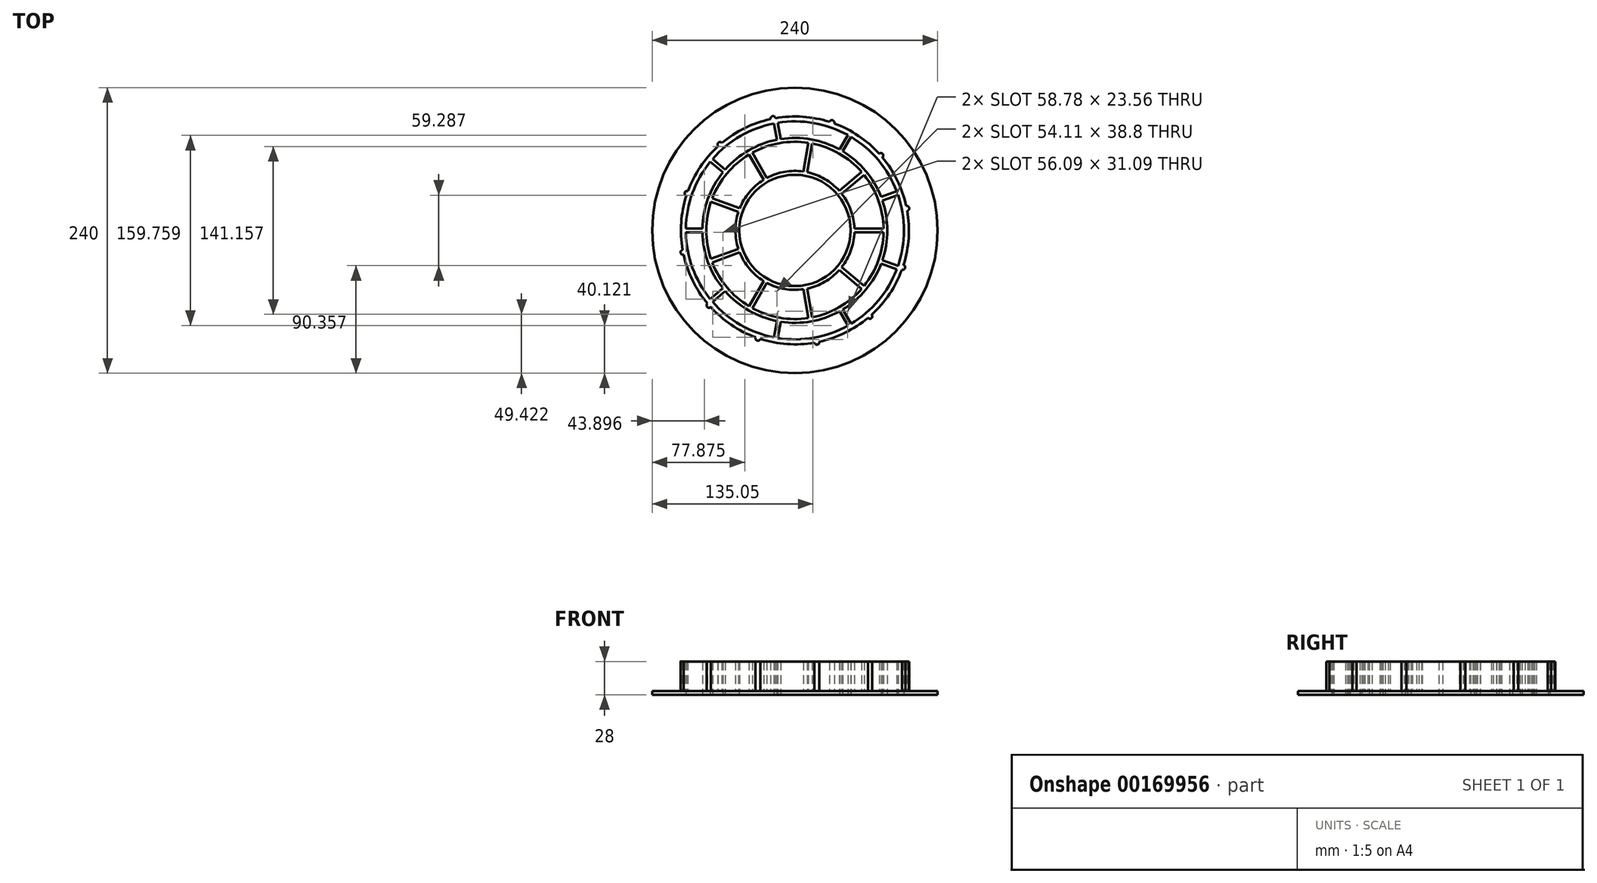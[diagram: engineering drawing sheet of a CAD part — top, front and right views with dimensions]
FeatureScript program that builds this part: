
annotation { "Feature Type Name" : "Feature", "Feature Type Description" : "" }
export const myFeature = defineFeature(function(context is Context, id is Id, definition is map)
    precondition{}
    {
        {
            var Q0;
            Q0=qCreatedBy(makeId("Top.planeOp"),FACE);
            var sketch = newSketch(context, id + "F0", { "sketchPlane" : qUnion([Q0])});
            skCircle(sketch, "E0", {"center": v(0, 0) * mm, "radius": 46.79 * mm});
            skCircle(sketch, "E1.0", {"center": v(0, 0) * mm, "radius": 49.98 * mm});
            skCircle(sketch, "E2", {"center": v(0, 0) * mm, "radius": 74.53 * mm});
            skCircle(sketch, "E3.0", {"center": v(0, 0) * mm, "radius": 77.73 * mm});
            skCircle(sketch, "E4", {"center": v(0, 0) * mm, "radius": 91.66 * mm});
            skCircle(sketch, "E5.0", {"center": v(0, 0) * mm, "radius": 95.78 * mm});
            skCircle(sketch, "E6", {"center": v(0, 0) * mm, "radius": 120 * mm});
            skLineSegment(sketch, "E7", {"start": v(46.79, 0) * mm, "end": v(77.72, 0) * mm, "construction": true});
            skLineSegment(sketch, "E8.0", {"start": v(46.79, -1.6) * mm, "end": v(77.99, -1.6) * mm});
            skLineSegment(sketch, "E9.0", {"start": v(46.79, 1.6) * mm, "end": v(77.99, 1.6) * mm});
            skLineSegment(sketch, "E10.1.0", {"start": v(34.81, 31.3) * mm, "end": v(58.71, 51.35) * mm});
            skLineSegment(sketch, "E10.1.1", {"start": v(35.84, 30.07) * mm, "end": v(59.54, 49.96) * mm, "construction": true});
            skLineSegment(sketch, "E10.1.2", {"start": v(36.87, 28.85) * mm, "end": v(60.77, 48.9) * mm});
            skLineSegment(sketch, "E10.2.0", {"start": v(6.55, 46.35) * mm, "end": v(11.97, 77.08) * mm});
            skLineSegment(sketch, "E10.2.1", {"start": v(8.12, 46.07) * mm, "end": v(13.5, 76.54) * mm, "construction": true});
            skLineSegment(sketch, "E10.2.2", {"start": v(9.7, 45.8) * mm, "end": v(15.12, 76.52) * mm});
            skLineSegment(sketch, "E10.3.0", {"start": v(-24.78, 39.72) * mm, "end": v(-40.38, 66.74) * mm});
            skLineSegment(sketch, "E10.3.1", {"start": v(-23.4, 40.52) * mm, "end": v(-38.86, 67.31) * mm, "construction": true});
            skLineSegment(sketch, "E10.3.2", {"start": v(-22, 41.32) * mm, "end": v(-37.6, 68.34) * mm});
            skLineSegment(sketch, "E10.4.0", {"start": v(-44.51, 14.5) * mm, "end": v(-73.83, 25.17) * mm});
            skLineSegment(sketch, "E10.4.1", {"start": v(-43.96, 16) * mm, "end": v(-73.04, 26.58) * mm, "construction": true});
            skLineSegment(sketch, "E10.4.2", {"start": v(-43.42, 17.5) * mm, "end": v(-72.74, 28.18) * mm});
            skLineSegment(sketch, "E10.5.0", {"start": v(-43.42, -17.5) * mm, "end": v(-72.74, -28.18) * mm});
            skLineSegment(sketch, "E10.5.1", {"start": v(-43.96, -16) * mm, "end": v(-73.04, -26.58) * mm, "construction": true});
            skLineSegment(sketch, "E10.5.2", {"start": v(-44.51, -14.5) * mm, "end": v(-73.83, -25.17) * mm});
            skLineSegment(sketch, "E10.6.0", {"start": v(-22, -41.32) * mm, "end": v(-37.6, -68.34) * mm});
            skLineSegment(sketch, "E10.6.1", {"start": v(-23.4, -40.52) * mm, "end": v(-38.86, -67.31) * mm, "construction": true});
            skLineSegment(sketch, "E10.6.2", {"start": v(-24.78, -39.72) * mm, "end": v(-40.38, -66.74) * mm});
            skLineSegment(sketch, "E10.7.0", {"start": v(9.7, -45.8) * mm, "end": v(15.12, -76.52) * mm});
            skLineSegment(sketch, "E10.7.1", {"start": v(8.12, -46.07) * mm, "end": v(13.5, -76.54) * mm, "construction": true});
            skLineSegment(sketch, "E10.7.2", {"start": v(6.55, -46.35) * mm, "end": v(11.97, -77.08) * mm});
            skLineSegment(sketch, "E10.8.0", {"start": v(36.87, -28.85) * mm, "end": v(60.77, -48.9) * mm});
            skLineSegment(sketch, "E10.8.1", {"start": v(35.84, -30.07) * mm, "end": v(59.54, -49.96) * mm, "construction": true});
            skLineSegment(sketch, "E10.8.2", {"start": v(34.81, -31.3) * mm, "end": v(58.71, -51.35) * mm});
            skPoint(sketch, "E11.center", {"position": v(-0.02, 0.04) * mm});
            skLineSegment(sketch, "E12", {"start": v(57.09, 47.9) * mm, "end": v(73.38, 61.57) * mm, "construction": true});
            skLineSegment(sketch, "E13.0", {"start": v(58.22, 46.76) * mm, "end": v(74.6, 60.51) * mm});
            skLineSegment(sketch, "E14.0", {"start": v(56.16, 49.21) * mm, "end": v(72.55, 62.96) * mm});
            skLineSegment(sketch, "E15.1.0", {"start": v(35.94, 65.45) * mm, "end": v(46.64, 83.98) * mm});
            skLineSegment(sketch, "E15.1.1", {"start": v(38.71, 63.85) * mm, "end": v(49.4, 82.38) * mm});
            skLineSegment(sketch, "E15.2.0", {"start": v(11.39, 73.8) * mm, "end": v(15.1, 94.86) * mm});
            skLineSegment(sketch, "E15.2.1", {"start": v(14.54, 73.24) * mm, "end": v(18.25, 94.3) * mm});
            skLineSegment(sketch, "E15.3.0", {"start": v(-14.54, 73.24) * mm, "end": v(-18.25, 94.3) * mm});
            skLineSegment(sketch, "E15.3.1", {"start": v(-11.39, 73.8) * mm, "end": v(-15.1, 94.86) * mm});
            skLineSegment(sketch, "E15.4.0", {"start": v(-38.71, 63.85) * mm, "end": v(-49.4, 82.38) * mm});
            skLineSegment(sketch, "E15.4.1", {"start": v(-35.94, 65.45) * mm, "end": v(-46.64, 83.98) * mm});
            skLineSegment(sketch, "E15.5.0", {"start": v(-58.22, 46.76) * mm, "end": v(-74.6, 60.51) * mm});
            skLineSegment(sketch, "E15.5.1", {"start": v(-56.16, 49.21) * mm, "end": v(-72.55, 62.96) * mm});
            skLineSegment(sketch, "E15.6.0", {"start": v(-70.7, 24.03) * mm, "end": v(-90.8, 31.35) * mm});
            skLineSegment(sketch, "E15.6.1", {"start": v(-69.6, 27.04) * mm, "end": v(-89.7, 34.35) * mm});
            skLineSegment(sketch, "E15.7.0", {"start": v(-74.66, -1.6) * mm, "end": v(-96.05, -1.6) * mm});
            skLineSegment(sketch, "E15.7.1", {"start": v(-74.66, 1.6) * mm, "end": v(-96.05, 1.6) * mm});
            skLineSegment(sketch, "E15.8.0", {"start": v(-69.6, -27.04) * mm, "end": v(-89.7, -34.35) * mm});
            skLineSegment(sketch, "E15.8.1", {"start": v(-70.7, -24.03) * mm, "end": v(-90.8, -31.35) * mm});
            skLineSegment(sketch, "E15.9.0", {"start": v(-56.16, -49.21) * mm, "end": v(-72.55, -62.96) * mm});
            skLineSegment(sketch, "E15.9.1", {"start": v(-58.22, -46.76) * mm, "end": v(-74.6, -60.51) * mm});
            skLineSegment(sketch, "E15.10.0", {"start": v(-35.94, -65.45) * mm, "end": v(-46.64, -83.98) * mm});
            skLineSegment(sketch, "E15.10.1", {"start": v(-38.71, -63.85) * mm, "end": v(-49.4, -82.38) * mm});
            skLineSegment(sketch, "E15.11.0", {"start": v(-11.39, -73.8) * mm, "end": v(-15.1, -94.86) * mm});
            skLineSegment(sketch, "E15.11.1", {"start": v(-14.54, -73.24) * mm, "end": v(-18.25, -94.3) * mm});
            skLineSegment(sketch, "E15.12.0", {"start": v(14.54, -73.24) * mm, "end": v(18.25, -94.3) * mm});
            skLineSegment(sketch, "E15.12.1", {"start": v(11.39, -73.8) * mm, "end": v(15.1, -94.86) * mm});
            skLineSegment(sketch, "E15.13.0", {"start": v(38.71, -63.85) * mm, "end": v(49.4, -82.38) * mm});
            skLineSegment(sketch, "E15.13.1", {"start": v(35.94, -65.45) * mm, "end": v(46.64, -83.98) * mm});
            skLineSegment(sketch, "E15.14.0", {"start": v(58.22, -46.76) * mm, "end": v(74.6, -60.51) * mm});
            skLineSegment(sketch, "E15.14.1", {"start": v(56.16, -49.21) * mm, "end": v(72.55, -62.96) * mm});
            skLineSegment(sketch, "E15.15.0", {"start": v(70.7, -24.03) * mm, "end": v(90.8, -31.35) * mm});
            skLineSegment(sketch, "E15.15.1", {"start": v(69.6, -27.04) * mm, "end": v(89.7, -34.35) * mm});
            skLineSegment(sketch, "E15.16.0", {"start": v(74.66, 1.6) * mm, "end": v(96.05, 1.6) * mm});
            skLineSegment(sketch, "E15.16.1", {"start": v(74.66, -1.6) * mm, "end": v(96.05, -1.6) * mm});
            skLineSegment(sketch, "E15.17.0", {"start": v(69.6, 27.04) * mm, "end": v(89.7, 34.35) * mm});
            skLineSegment(sketch, "E15.17.1", {"start": v(70.7, 24.03) * mm, "end": v(90.8, 31.35) * mm});
            skCircle(sketch, "E16", {"center": v(94, 18.42) * mm, "radius": 2.1 * mm});
            skCircle(sketch, "E17.1.0", {"center": v(72.2, 62.95) * mm, "radius": 2.1 * mm});
            skCircle(sketch, "E17.2.0", {"center": v(31.04, 90.61) * mm, "radius": 2.1 * mm});
            skCircle(sketch, "E17.3.0", {"center": v(-18.42, 94) * mm, "radius": 2.1 * mm});
            skCircle(sketch, "E17.4.0", {"center": v(-62.95, 72.2) * mm, "radius": 2.1 * mm});
            skCircle(sketch, "E17.5.0", {"center": v(-90.61, 31.04) * mm, "radius": 2.1 * mm});
            skCircle(sketch, "E17.6.0", {"center": v(-94, -18.42) * mm, "radius": 2.1 * mm});
            skCircle(sketch, "E17.7.0", {"center": v(-72.2, -62.95) * mm, "radius": 2.1 * mm});
            skCircle(sketch, "E17.8.0", {"center": v(-31.04, -90.61) * mm, "radius": 2.1 * mm});
            skCircle(sketch, "E17.9.0", {"center": v(18.42, -94) * mm, "radius": 2.1 * mm});
            skCircle(sketch, "E17.10.0", {"center": v(62.95, -72.2) * mm, "radius": 2.1 * mm});
            skCircle(sketch, "E17.11.0", {"center": v(90.61, -31.04) * mm, "radius": 2.1 * mm});
            skSolve(sketch);
        }
        {
            var Q0;
            {var subQ0=sQuery(id+"F0.wireOp",EDGE,"E8.0");var subQ1=sQuery(id+"F0.wireOp",EDGE,"E2");var subQ2=makeQuery(id+"F0.imprint","INTERSECT",VERTEX,{"derivedFrom":[subQ1,subQ0]});Q0=makeQuery(id+"F0.imprint","IMPRINT",FACE,{"disambiguationData":[TD([[makeQuery(id+"F0.imprint","IMPRINT",EDGE,{"disambiguationData":[TD([[subQ2,1.0]])],"derivedFrom":subQ1}),-1.0]])]});}
            var Q1;
            Q1=makeQuery(id+"F0.imprint","IMPRINT",FACE,{"disambiguationData":[TD([[makeQuery(id+"F0.imprint","IMPRINT",EDGE,{"derivedFrom":sQuery(id+"F0.wireOp",EDGE,"E4")}),-1.0]])]});
            var Q2;
            {var subQ0=sQuery(id+"F0.wireOp",EDGE,"E8.0");var subQ1=sQuery(id+"F0.wireOp",EDGE,"E2");var subQ2=makeQuery(id+"F0.imprint","INTERSECT",VERTEX,{"derivedFrom":[subQ1,subQ0]});Q2=makeQuery(id+"F0.imprint","IMPRINT",FACE,{"disambiguationData":[TD([[makeQuery(id+"F0.imprint","IMPRINT",EDGE,{"disambiguationData":[TD([[subQ2,-1.0]])],"derivedFrom":subQ1}),-1.0]])]});}
            var Q3;
            {var subQ0=sQuery(id+"F0.wireOp",EDGE,"E8.0");var subQ1=sQuery(id+"F0.wireOp",EDGE,"E1.0");var subQ2=makeQuery(id+"F0.imprint","INTERSECT",VERTEX,{"derivedFrom":[subQ1,subQ0]});Q3=makeQuery(id+"F0.imprint","IMPRINT",FACE,{"disambiguationData":[TD([[makeQuery(id+"F0.imprint","IMPRINT",EDGE,{"disambiguationData":[TD([[subQ2,-1.0]])],"derivedFrom":subQ1}),-1.0]])]});}
            var Q4;
            {var subQ1=sQuery(id+"F0.wireOp",EDGE,"E10.1.2");var subQ3=sQuery(id+"F0.wireOp",EDGE,"E2");var subQ4=makeQuery(id+"F0.imprint","INTERSECT",VERTEX,{"derivedFrom":[subQ3,subQ1]});Q4=makeQuery(id+"F0.imprint","IMPRINT",FACE,{"disambiguationData":[TD([[makeQuery(id+"F0.imprint","IMPRINT",EDGE,{"disambiguationData":[TD([[subQ4,1.0]])],"derivedFrom":subQ3}),-1.0]])]});}
            var Q5;
            {var subQ0=sQuery(id+"F0.wireOp",EDGE,"E13.0");var subQ1=makeQuery(id+"F0.imprint","IMPRINT",VERTEX,{"derivedFrom":subQ0});Q5=makeQuery(id+"F0.imprint","IMPRINT",FACE,{"disambiguationData":[TD([[makeQuery(id+"F0.imprint","IMPRINT",EDGE,{"disambiguationData":[TD([[subQ1,1.0]])],"derivedFrom":subQ0}),1.0]])]});}
            var Q6;
            {var subQ0=sQuery(id+"F0.wireOp",EDGE,"E10.1.2");var subQ1=sQuery(id+"F0.wireOp",EDGE,"E1.0");var subQ2=makeQuery(id+"F0.imprint","INTERSECT",VERTEX,{"derivedFrom":[subQ1,subQ0]});Q6=makeQuery(id+"F0.imprint","IMPRINT",FACE,{"disambiguationData":[TD([[makeQuery(id+"F0.imprint","IMPRINT",EDGE,{"disambiguationData":[TD([[subQ2,-1.0]])],"derivedFrom":subQ1}),-1.0]])]});}
            var Q7;
            {var subQ1=sQuery(id+"F0.wireOp",EDGE,"E10.1.2");var subQ3=sQuery(id+"F0.wireOp",EDGE,"E2");var subQ4=makeQuery(id+"F0.imprint","INTERSECT",VERTEX,{"derivedFrom":[subQ3,subQ1]});Q7=makeQuery(id+"F0.imprint","IMPRINT",FACE,{"disambiguationData":[TD([[makeQuery(id+"F0.imprint","IMPRINT",EDGE,{"disambiguationData":[TD([[subQ4,-1.0]])],"derivedFrom":subQ3}),-1.0]])]});}
            var Q8;
            {var subQ3=sQuery(id+"F0.wireOp",EDGE,"E2");var subQ7=sQuery(id+"F0.wireOp",EDGE,"E10.1.0");var subQ8=makeQuery(id+"F0.imprint","INTERSECT",VERTEX,{"derivedFrom":[subQ3,subQ7]});Q8=makeQuery(id+"F0.imprint","IMPRINT",FACE,{"disambiguationData":[TD([[makeQuery(id+"F0.imprint","IMPRINT",EDGE,{"disambiguationData":[TD([[subQ8,-1.0]])],"derivedFrom":subQ3}),-1.0]])]});}
            var Q9;
            {var subQ0=sQuery(id+"F0.wireOp",EDGE,"E10.2.2");var subQ1=sQuery(id+"F0.wireOp",EDGE,"E1.0");var subQ2=makeQuery(id+"F0.imprint","INTERSECT",VERTEX,{"derivedFrom":[subQ1,subQ0]});Q9=makeQuery(id+"F0.imprint","IMPRINT",FACE,{"disambiguationData":[TD([[makeQuery(id+"F0.imprint","IMPRINT",EDGE,{"disambiguationData":[TD([[subQ2,-1.0]])],"derivedFrom":subQ1}),-1.0]])]});}
            var Q10;
            {var subQ0=sQuery(id+"F0.wireOp",EDGE,"E10.2.2");var subQ1=sQuery(id+"F0.wireOp",EDGE,"E2");var subQ2=makeQuery(id+"F0.imprint","INTERSECT",VERTEX,{"derivedFrom":[subQ1,subQ0]});Q10=makeQuery(id+"F0.imprint","IMPRINT",FACE,{"disambiguationData":[TD([[makeQuery(id+"F0.imprint","IMPRINT",EDGE,{"disambiguationData":[TD([[subQ2,-1.0]])],"derivedFrom":subQ1}),-1.0]])]});}
            var Q11;
            {var subQ0=sQuery(id+"F0.wireOp",EDGE,"E10.2.0");var subQ1=sQuery(id+"F0.wireOp",EDGE,"E2");var subQ2=makeQuery(id+"F0.imprint","INTERSECT",VERTEX,{"derivedFrom":[subQ1,subQ0]});Q11=makeQuery(id+"F0.imprint","IMPRINT",FACE,{"disambiguationData":[TD([[makeQuery(id+"F0.imprint","IMPRINT",EDGE,{"disambiguationData":[TD([[subQ2,-1.0]])],"derivedFrom":subQ1}),-1.0]])]});}
            var Q12;
            {var subQ0=sQuery(id+"F0.wireOp",EDGE,"E10.3.2");var subQ1=sQuery(id+"F0.wireOp",EDGE,"E2");var subQ2=makeQuery(id+"F0.imprint","INTERSECT",VERTEX,{"derivedFrom":[subQ1,subQ0]});Q12=makeQuery(id+"F0.imprint","IMPRINT",FACE,{"disambiguationData":[TD([[makeQuery(id+"F0.imprint","IMPRINT",EDGE,{"disambiguationData":[TD([[subQ2,-1.0]])],"derivedFrom":subQ1}),-1.0]])]});}
            var Q13;
            {var subQ0=sQuery(id+"F0.wireOp",EDGE,"E10.3.2");var subQ1=sQuery(id+"F0.wireOp",EDGE,"E1.0");var subQ2=makeQuery(id+"F0.imprint","INTERSECT",VERTEX,{"derivedFrom":[subQ1,subQ0]});Q13=makeQuery(id+"F0.imprint","IMPRINT",FACE,{"disambiguationData":[TD([[makeQuery(id+"F0.imprint","IMPRINT",EDGE,{"disambiguationData":[TD([[subQ2,-1.0]])],"derivedFrom":subQ1}),-1.0]])]});}
            var Q14;
            {var subQ0=sQuery(id+"F0.wireOp",EDGE,"E10.3.0");var subQ1=sQuery(id+"F0.wireOp",EDGE,"E2");var subQ2=makeQuery(id+"F0.imprint","INTERSECT",VERTEX,{"derivedFrom":[subQ1,subQ0]});Q14=makeQuery(id+"F0.imprint","IMPRINT",FACE,{"disambiguationData":[TD([[makeQuery(id+"F0.imprint","IMPRINT",EDGE,{"disambiguationData":[TD([[subQ2,-1.0]])],"derivedFrom":subQ1}),-1.0]])]});}
            var Q15;
            {var subQ0=sQuery(id+"F0.wireOp",EDGE,"E10.4.2");var subQ1=sQuery(id+"F0.wireOp",EDGE,"E2");var subQ2=makeQuery(id+"F0.imprint","INTERSECT",VERTEX,{"derivedFrom":[subQ1,subQ0]});Q15=makeQuery(id+"F0.imprint","IMPRINT",FACE,{"disambiguationData":[TD([[makeQuery(id+"F0.imprint","IMPRINT",EDGE,{"disambiguationData":[TD([[subQ2,-1.0]])],"derivedFrom":subQ1}),-1.0]])]});}
            var Q16;
            {var subQ0=sQuery(id+"F0.wireOp",EDGE,"E10.4.2");var subQ1=sQuery(id+"F0.wireOp",EDGE,"E1.0");var subQ2=makeQuery(id+"F0.imprint","INTERSECT",VERTEX,{"derivedFrom":[subQ1,subQ0]});Q16=makeQuery(id+"F0.imprint","IMPRINT",FACE,{"disambiguationData":[TD([[makeQuery(id+"F0.imprint","IMPRINT",EDGE,{"disambiguationData":[TD([[subQ2,-1.0]])],"derivedFrom":subQ1}),-1.0]])]});}
            var Q17;
            {var subQ0=sQuery(id+"F0.wireOp",EDGE,"E10.4.0");var subQ1=sQuery(id+"F0.wireOp",EDGE,"E2");var subQ2=makeQuery(id+"F0.imprint","INTERSECT",VERTEX,{"derivedFrom":[subQ1,subQ0]});Q17=makeQuery(id+"F0.imprint","IMPRINT",FACE,{"disambiguationData":[TD([[makeQuery(id+"F0.imprint","IMPRINT",EDGE,{"disambiguationData":[TD([[subQ2,-1.0]])],"derivedFrom":subQ1}),-1.0]])]});}
            var Q18;
            {var subQ0=sQuery(id+"F0.wireOp",EDGE,"E10.5.2");var subQ1=sQuery(id+"F0.wireOp",EDGE,"E1.0");var subQ2=makeQuery(id+"F0.imprint","INTERSECT",VERTEX,{"derivedFrom":[subQ1,subQ0]});Q18=makeQuery(id+"F0.imprint","IMPRINT",FACE,{"disambiguationData":[TD([[makeQuery(id+"F0.imprint","IMPRINT",EDGE,{"disambiguationData":[TD([[subQ2,-1.0]])],"derivedFrom":subQ1}),-1.0]])]});}
            var Q19;
            {var subQ0=sQuery(id+"F0.wireOp",EDGE,"E10.5.2");var subQ1=sQuery(id+"F0.wireOp",EDGE,"E2");var subQ2=makeQuery(id+"F0.imprint","INTERSECT",VERTEX,{"derivedFrom":[subQ1,subQ0]});Q19=makeQuery(id+"F0.imprint","IMPRINT",FACE,{"disambiguationData":[TD([[makeQuery(id+"F0.imprint","IMPRINT",EDGE,{"disambiguationData":[TD([[subQ2,-1.0]])],"derivedFrom":subQ1}),-1.0]])]});}
            var Q20;
            {var subQ0=sQuery(id+"F0.wireOp",EDGE,"E10.5.0");var subQ1=sQuery(id+"F0.wireOp",EDGE,"E2");var subQ2=makeQuery(id+"F0.imprint","INTERSECT",VERTEX,{"derivedFrom":[subQ1,subQ0]});Q20=makeQuery(id+"F0.imprint","IMPRINT",FACE,{"disambiguationData":[TD([[makeQuery(id+"F0.imprint","IMPRINT",EDGE,{"disambiguationData":[TD([[subQ2,-1.0]])],"derivedFrom":subQ1}),-1.0]])]});}
            var Q21;
            {var subQ0=sQuery(id+"F0.wireOp",EDGE,"E10.6.2");var subQ1=sQuery(id+"F0.wireOp",EDGE,"E1.0");var subQ2=makeQuery(id+"F0.imprint","INTERSECT",VERTEX,{"derivedFrom":[subQ1,subQ0]});Q21=makeQuery(id+"F0.imprint","IMPRINT",FACE,{"disambiguationData":[TD([[makeQuery(id+"F0.imprint","IMPRINT",EDGE,{"disambiguationData":[TD([[subQ2,-1.0]])],"derivedFrom":subQ1}),-1.0]])]});}
            var Q22;
            {var subQ0=sQuery(id+"F0.wireOp",EDGE,"E10.6.2");var subQ1=sQuery(id+"F0.wireOp",EDGE,"E2");var subQ2=makeQuery(id+"F0.imprint","INTERSECT",VERTEX,{"derivedFrom":[subQ1,subQ0]});Q22=makeQuery(id+"F0.imprint","IMPRINT",FACE,{"disambiguationData":[TD([[makeQuery(id+"F0.imprint","IMPRINT",EDGE,{"disambiguationData":[TD([[subQ2,-1.0]])],"derivedFrom":subQ1}),-1.0]])]});}
            var Q23;
            {var subQ0=sQuery(id+"F0.wireOp",EDGE,"E10.6.0");var subQ1=sQuery(id+"F0.wireOp",EDGE,"E2");var subQ2=makeQuery(id+"F0.imprint","INTERSECT",VERTEX,{"derivedFrom":[subQ1,subQ0]});Q23=makeQuery(id+"F0.imprint","IMPRINT",FACE,{"disambiguationData":[TD([[makeQuery(id+"F0.imprint","IMPRINT",EDGE,{"disambiguationData":[TD([[subQ2,-1.0]])],"derivedFrom":subQ1}),-1.0]])]});}
            var Q24;
            {var subQ0=sQuery(id+"F0.wireOp",EDGE,"E10.7.2");var subQ1=sQuery(id+"F0.wireOp",EDGE,"E1.0");var subQ2=makeQuery(id+"F0.imprint","INTERSECT",VERTEX,{"derivedFrom":[subQ1,subQ0]});Q24=makeQuery(id+"F0.imprint","IMPRINT",FACE,{"disambiguationData":[TD([[makeQuery(id+"F0.imprint","IMPRINT",EDGE,{"disambiguationData":[TD([[subQ2,-1.0]])],"derivedFrom":subQ1}),-1.0]])]});}
            var Q25;
            {var subQ0=sQuery(id+"F0.wireOp",EDGE,"E10.7.2");var subQ1=sQuery(id+"F0.wireOp",EDGE,"E2");var subQ2=makeQuery(id+"F0.imprint","INTERSECT",VERTEX,{"derivedFrom":[subQ1,subQ0]});Q25=makeQuery(id+"F0.imprint","IMPRINT",FACE,{"disambiguationData":[TD([[makeQuery(id+"F0.imprint","IMPRINT",EDGE,{"disambiguationData":[TD([[subQ2,-1.0]])],"derivedFrom":subQ1}),-1.0]])]});}
            var Q26;
            {var subQ0=sQuery(id+"F0.wireOp",EDGE,"E10.7.0");var subQ1=sQuery(id+"F0.wireOp",EDGE,"E2");var subQ2=makeQuery(id+"F0.imprint","INTERSECT",VERTEX,{"derivedFrom":[subQ1,subQ0]});Q26=makeQuery(id+"F0.imprint","IMPRINT",FACE,{"disambiguationData":[TD([[makeQuery(id+"F0.imprint","IMPRINT",EDGE,{"disambiguationData":[TD([[subQ2,-1.0]])],"derivedFrom":subQ1}),-1.0]])]});}
            var Q27;
            {var subQ0=sQuery(id+"F0.wireOp",EDGE,"E10.8.2");var subQ1=sQuery(id+"F0.wireOp",EDGE,"E1.0");var subQ2=makeQuery(id+"F0.imprint","INTERSECT",VERTEX,{"derivedFrom":[subQ1,subQ0]});Q27=makeQuery(id+"F0.imprint","IMPRINT",FACE,{"disambiguationData":[TD([[makeQuery(id+"F0.imprint","IMPRINT",EDGE,{"disambiguationData":[TD([[subQ2,-1.0]])],"derivedFrom":subQ1}),-1.0]])]});}
            var Q28;
            {var subQ0=sQuery(id+"F0.wireOp",EDGE,"E10.8.2");var subQ1=sQuery(id+"F0.wireOp",EDGE,"E2");var subQ2=makeQuery(id+"F0.imprint","INTERSECT",VERTEX,{"derivedFrom":[subQ1,subQ0]});Q28=makeQuery(id+"F0.imprint","IMPRINT",FACE,{"disambiguationData":[TD([[makeQuery(id+"F0.imprint","IMPRINT",EDGE,{"disambiguationData":[TD([[subQ2,-1.0]])],"derivedFrom":subQ1}),-1.0]])]});}
            var Q29;
            {var subQ0=sQuery(id+"F0.wireOp",EDGE,"E15.17.1");var subQ1=sQuery(id+"F0.wireOp",EDGE,"E3.0");var subQ2=makeQuery(id+"F0.imprint","INTERSECT",VERTEX,{"derivedFrom":[subQ1,subQ0]});Q29=makeQuery(id+"F0.imprint","IMPRINT",FACE,{"disambiguationData":[TD([[makeQuery(id+"F0.imprint","IMPRINT",EDGE,{"disambiguationData":[TD([[subQ2,-1.0]])],"derivedFrom":subQ1}),-1.0]])]});}
            var Q30;
            {var subQ0=sQuery(id+"F0.wireOp",EDGE,"E15.16.0");var subQ1=makeQuery(id+"F0.imprint","IMPRINT",VERTEX,{"derivedFrom":subQ0});Q30=makeQuery(id+"F0.imprint","IMPRINT",FACE,{"disambiguationData":[TD([[makeQuery(id+"F0.imprint","IMPRINT",EDGE,{"disambiguationData":[TD([[subQ1,1.0]])],"derivedFrom":subQ0}),-1.0]])]});}
            var Q31;
            {var subQ0=sQuery(id+"F0.wireOp",EDGE,"E15.15.1");var subQ1=sQuery(id+"F0.wireOp",EDGE,"E3.0");var subQ2=makeQuery(id+"F0.imprint","INTERSECT",VERTEX,{"derivedFrom":[subQ1,subQ0]});Q31=makeQuery(id+"F0.imprint","IMPRINT",FACE,{"disambiguationData":[TD([[makeQuery(id+"F0.imprint","IMPRINT",EDGE,{"disambiguationData":[TD([[subQ2,-1.0]])],"derivedFrom":subQ1}),-1.0]])]});}
            var Q32;
            {var subQ0=sQuery(id+"F0.wireOp",EDGE,"E15.14.0");var subQ1=makeQuery(id+"F0.imprint","IMPRINT",VERTEX,{"derivedFrom":subQ0});Q32=makeQuery(id+"F0.imprint","IMPRINT",FACE,{"disambiguationData":[TD([[makeQuery(id+"F0.imprint","IMPRINT",EDGE,{"disambiguationData":[TD([[subQ1,1.0]])],"derivedFrom":subQ0}),-1.0]])]});}
            var Q33;
            {var subQ0=sQuery(id+"F0.wireOp",EDGE,"E15.13.1");var subQ1=sQuery(id+"F0.wireOp",EDGE,"E3.0");var subQ2=makeQuery(id+"F0.imprint","INTERSECT",VERTEX,{"derivedFrom":[subQ1,subQ0]});Q33=makeQuery(id+"F0.imprint","IMPRINT",FACE,{"disambiguationData":[TD([[makeQuery(id+"F0.imprint","IMPRINT",EDGE,{"disambiguationData":[TD([[subQ2,-1.0]])],"derivedFrom":subQ1}),-1.0]])]});}
            var Q34;
            {var subQ0=sQuery(id+"F0.wireOp",EDGE,"E15.12.0");var subQ1=makeQuery(id+"F0.imprint","IMPRINT",VERTEX,{"derivedFrom":subQ0});Q34=makeQuery(id+"F0.imprint","IMPRINT",FACE,{"disambiguationData":[TD([[makeQuery(id+"F0.imprint","IMPRINT",EDGE,{"disambiguationData":[TD([[subQ1,1.0]])],"derivedFrom":subQ0}),-1.0]])]});}
            var Q35;
            {var subQ0=sQuery(id+"F0.wireOp",EDGE,"E15.11.1");var subQ1=sQuery(id+"F0.wireOp",EDGE,"E3.0");var subQ2=makeQuery(id+"F0.imprint","INTERSECT",VERTEX,{"derivedFrom":[subQ1,subQ0]});Q35=makeQuery(id+"F0.imprint","IMPRINT",FACE,{"disambiguationData":[TD([[makeQuery(id+"F0.imprint","IMPRINT",EDGE,{"disambiguationData":[TD([[subQ2,-1.0]])],"derivedFrom":subQ1}),-1.0]])]});}
            var Q36;
            {var subQ0=sQuery(id+"F0.wireOp",EDGE,"E15.10.0");var subQ1=makeQuery(id+"F0.imprint","IMPRINT",VERTEX,{"derivedFrom":subQ0});Q36=makeQuery(id+"F0.imprint","IMPRINT",FACE,{"disambiguationData":[TD([[makeQuery(id+"F0.imprint","IMPRINT",EDGE,{"disambiguationData":[TD([[subQ1,1.0]])],"derivedFrom":subQ0}),-1.0]])]});}
            var Q37;
            {var subQ0=sQuery(id+"F0.wireOp",EDGE,"E15.9.1");var subQ1=sQuery(id+"F0.wireOp",EDGE,"E3.0");var subQ2=makeQuery(id+"F0.imprint","INTERSECT",VERTEX,{"derivedFrom":[subQ1,subQ0]});Q37=makeQuery(id+"F0.imprint","IMPRINT",FACE,{"disambiguationData":[TD([[makeQuery(id+"F0.imprint","IMPRINT",EDGE,{"disambiguationData":[TD([[subQ2,-1.0]])],"derivedFrom":subQ1}),-1.0]])]});}
            var Q38;
            {var subQ0=sQuery(id+"F0.wireOp",EDGE,"E15.8.0");var subQ1=makeQuery(id+"F0.imprint","IMPRINT",VERTEX,{"derivedFrom":subQ0});Q38=makeQuery(id+"F0.imprint","IMPRINT",FACE,{"disambiguationData":[TD([[makeQuery(id+"F0.imprint","IMPRINT",EDGE,{"disambiguationData":[TD([[subQ1,1.0]])],"derivedFrom":subQ0}),-1.0]])]});}
            var Q39;
            {var subQ0=sQuery(id+"F0.wireOp",EDGE,"E15.7.1");var subQ1=sQuery(id+"F0.wireOp",EDGE,"E3.0");var subQ2=makeQuery(id+"F0.imprint","INTERSECT",VERTEX,{"derivedFrom":[subQ1,subQ0]});Q39=makeQuery(id+"F0.imprint","IMPRINT",FACE,{"disambiguationData":[TD([[makeQuery(id+"F0.imprint","IMPRINT",EDGE,{"disambiguationData":[TD([[subQ2,-1.0]])],"derivedFrom":subQ1}),-1.0]])]});}
            var Q40;
            {var subQ0=sQuery(id+"F0.wireOp",EDGE,"E15.6.0");var subQ1=makeQuery(id+"F0.imprint","IMPRINT",VERTEX,{"derivedFrom":subQ0});Q40=makeQuery(id+"F0.imprint","IMPRINT",FACE,{"disambiguationData":[TD([[makeQuery(id+"F0.imprint","IMPRINT",EDGE,{"disambiguationData":[TD([[subQ1,1.0]])],"derivedFrom":subQ0}),-1.0]])]});}
            var Q41;
            {var subQ0=sQuery(id+"F0.wireOp",EDGE,"E15.5.1");var subQ1=sQuery(id+"F0.wireOp",EDGE,"E3.0");var subQ2=makeQuery(id+"F0.imprint","INTERSECT",VERTEX,{"derivedFrom":[subQ1,subQ0]});Q41=makeQuery(id+"F0.imprint","IMPRINT",FACE,{"disambiguationData":[TD([[makeQuery(id+"F0.imprint","IMPRINT",EDGE,{"disambiguationData":[TD([[subQ2,-1.0]])],"derivedFrom":subQ1}),-1.0]])]});}
            var Q42;
            {var subQ0=sQuery(id+"F0.wireOp",EDGE,"E15.4.0");var subQ1=makeQuery(id+"F0.imprint","IMPRINT",VERTEX,{"derivedFrom":subQ0});Q42=makeQuery(id+"F0.imprint","IMPRINT",FACE,{"disambiguationData":[TD([[makeQuery(id+"F0.imprint","IMPRINT",EDGE,{"disambiguationData":[TD([[subQ1,1.0]])],"derivedFrom":subQ0}),-1.0]])]});}
            var Q43;
            {var subQ0=sQuery(id+"F0.wireOp",EDGE,"E15.3.1");var subQ1=sQuery(id+"F0.wireOp",EDGE,"E3.0");var subQ2=makeQuery(id+"F0.imprint","INTERSECT",VERTEX,{"derivedFrom":[subQ1,subQ0]});Q43=makeQuery(id+"F0.imprint","IMPRINT",FACE,{"disambiguationData":[TD([[makeQuery(id+"F0.imprint","IMPRINT",EDGE,{"disambiguationData":[TD([[subQ2,-1.0]])],"derivedFrom":subQ1}),-1.0]])]});}
            var Q44;
            {var subQ0=sQuery(id+"F0.wireOp",EDGE,"E15.2.0");var subQ1=makeQuery(id+"F0.imprint","IMPRINT",VERTEX,{"derivedFrom":subQ0});Q44=makeQuery(id+"F0.imprint","IMPRINT",FACE,{"disambiguationData":[TD([[makeQuery(id+"F0.imprint","IMPRINT",EDGE,{"disambiguationData":[TD([[subQ1,1.0]])],"derivedFrom":subQ0}),-1.0]])]});}
            var Q45;
            {var subQ0=sQuery(id+"F0.wireOp",EDGE,"E15.1.1");var subQ1=sQuery(id+"F0.wireOp",EDGE,"E3.0");var subQ2=makeQuery(id+"F0.imprint","INTERSECT",VERTEX,{"derivedFrom":[subQ1,subQ0]});Q45=makeQuery(id+"F0.imprint","IMPRINT",FACE,{"disambiguationData":[TD([[makeQuery(id+"F0.imprint","IMPRINT",EDGE,{"disambiguationData":[TD([[subQ2,-1.0]])],"derivedFrom":subQ1}),-1.0]])]});}
            var Q46;
            {var subQ0=sQuery(id+"F0.wireOp",EDGE,"E15.4.0");var subQ3=sQuery(id+"F0.wireOp",EDGE,"E4");var subQ4=makeQuery(id+"F0.imprint","INTERSECT",VERTEX,{"derivedFrom":[subQ3,subQ0]});Q46=makeQuery(id+"F0.imprint","IMPRINT",FACE,{"disambiguationData":[TD([[makeQuery(id+"F0.imprint","IMPRINT",EDGE,{"disambiguationData":[TD([[subQ4,-1.0]])],"derivedFrom":subQ3}),-1.0]])]});}
            var Q47;
            {var subQ0=sQuery(id+"F0.wireOp",EDGE,"E17.4.0");var subQ1=sQuery(id+"F0.wireOp",EDGE,"E5.0");var subQ2=makeQuery(id+"F0.imprint","INTERSECT",VERTEX,{"disambiguationData":[OD(0.0)],"derivedFrom":[subQ1,subQ0]});Q47=makeQuery(id+"F0.imprint","IMPRINT",FACE,{"disambiguationData":[TD([[makeQuery(id+"F0.imprint","IMPRINT",EDGE,{"disambiguationData":[TD([[subQ2,-1.0]])],"derivedFrom":subQ1}),-1.0]])]});}
            var Q48;
            {var subQ0=sQuery(id+"F0.wireOp",EDGE,"E15.6.0");var subQ1=sQuery(id+"F0.wireOp",EDGE,"E4");var subQ2=makeQuery(id+"F0.imprint","INTERSECT",VERTEX,{"derivedFrom":[subQ1,subQ0]});Q48=makeQuery(id+"F0.imprint","IMPRINT",FACE,{"disambiguationData":[TD([[makeQuery(id+"F0.imprint","IMPRINT",EDGE,{"disambiguationData":[TD([[subQ2,-1.0]])],"derivedFrom":subQ1}),-1.0]])]});}
            var Q49;
            {var subQ0=sQuery(id+"F0.wireOp",EDGE,"E15.6.1");var subQ3=sQuery(id+"F0.wireOp",EDGE,"E4");var subQ4=makeQuery(id+"F0.imprint","INTERSECT",VERTEX,{"derivedFrom":[subQ3,subQ0]});Q49=makeQuery(id+"F0.imprint","IMPRINT",FACE,{"disambiguationData":[TD([[makeQuery(id+"F0.imprint","IMPRINT",EDGE,{"disambiguationData":[TD([[subQ4,-1.0]])],"derivedFrom":subQ3}),-1.0]])]});}
            var Q50;
            {var subQ0=sQuery(id+"F0.wireOp",EDGE,"E5.0");var subQ1=makeQuery(id+"F0.imprint","INTERSECT",VERTEX,{"derivedFrom":[subQ0,sQuery(id+"F0.wireOp",EDGE,"E15.6.0")]});Q50=makeQuery(id+"F0.imprint","IMPRINT",FACE,{"disambiguationData":[TD([[makeQuery(id+"F0.imprint","IMPRINT",EDGE,{"disambiguationData":[TD([[subQ1,1.0]])],"derivedFrom":subQ0}),-1.0]])]});}
            var Q51;
            {var subQ0=sQuery(id+"F0.wireOp",EDGE,"E15.6.0");var subQ1=sQuery(id+"F0.wireOp",EDGE,"E5.0");var subQ2=makeQuery(id+"F0.imprint","INTERSECT",VERTEX,{"derivedFrom":[subQ1,subQ0]});Q51=makeQuery(id+"F0.imprint","IMPRINT",FACE,{"disambiguationData":[TD([[makeQuery(id+"F0.imprint","IMPRINT",EDGE,{"disambiguationData":[TD([[subQ2,-1.0]])],"derivedFrom":subQ1}),1.0]])]});}
            var Q52;
            {var subQ0=sQuery(id+"F0.wireOp",EDGE,"E15.6.0");var subQ1=sQuery(id+"F0.wireOp",EDGE,"E5.0");var subQ2=makeQuery(id+"F0.imprint","INTERSECT",VERTEX,{"derivedFrom":[subQ1,subQ0]});Q52=makeQuery(id+"F0.imprint","IMPRINT",FACE,{"disambiguationData":[TD([[makeQuery(id+"F0.imprint","IMPRINT",EDGE,{"disambiguationData":[TD([[subQ2,1.0]])],"derivedFrom":subQ1}),1.0]])]});}
            var Q53;
            {var subQ0=sQuery(id+"F0.wireOp",EDGE,"E17.4.0");var subQ1=sQuery(id+"F0.wireOp",EDGE,"E5.0");var subQ2=makeQuery(id+"F0.imprint","INTERSECT",VERTEX,{"disambiguationData":[OD(0.0)],"derivedFrom":[subQ1,subQ0]});Q53=makeQuery(id+"F0.imprint","IMPRINT",FACE,{"disambiguationData":[TD([[makeQuery(id+"F0.imprint","IMPRINT",EDGE,{"disambiguationData":[TD([[subQ2,-1.0]])],"derivedFrom":subQ1}),1.0]])]});}
            var Q54;
            {var subQ0=sQuery(id+"F0.wireOp",EDGE,"E15.3.0");var subQ1=sQuery(id+"F0.wireOp",EDGE,"E4");var subQ2=makeQuery(id+"F0.imprint","INTERSECT",VERTEX,{"derivedFrom":[subQ1,subQ0]});Q54=makeQuery(id+"F0.imprint","IMPRINT",FACE,{"disambiguationData":[TD([[makeQuery(id+"F0.imprint","IMPRINT",EDGE,{"disambiguationData":[TD([[subQ2,-1.0]])],"derivedFrom":subQ1}),-1.0]])]});}
            var Q55;
            {var subQ0=sQuery(id+"F0.wireOp",EDGE,"E15.3.1");var subQ3=sQuery(id+"F0.wireOp",EDGE,"E4");var subQ4=makeQuery(id+"F0.imprint","INTERSECT",VERTEX,{"derivedFrom":[subQ3,subQ0]});Q55=makeQuery(id+"F0.imprint","IMPRINT",FACE,{"disambiguationData":[TD([[makeQuery(id+"F0.imprint","IMPRINT",EDGE,{"disambiguationData":[TD([[subQ4,-1.0]])],"derivedFrom":subQ3}),-1.0]])]});}
            var Q56;
            {var subQ0=sQuery(id+"F0.wireOp",EDGE,"E5.0");var subQ1=makeQuery(id+"F0.imprint","INTERSECT",VERTEX,{"derivedFrom":[subQ0,sQuery(id+"F0.wireOp",EDGE,"E15.3.0")]});Q56=makeQuery(id+"F0.imprint","IMPRINT",FACE,{"disambiguationData":[TD([[makeQuery(id+"F0.imprint","IMPRINT",EDGE,{"disambiguationData":[TD([[subQ1,1.0]])],"derivedFrom":subQ0}),-1.0]])]});}
            var Q57;
            {var subQ0=sQuery(id+"F0.wireOp",EDGE,"E15.3.0");var subQ1=sQuery(id+"F0.wireOp",EDGE,"E5.0");var subQ2=makeQuery(id+"F0.imprint","INTERSECT",VERTEX,{"derivedFrom":[subQ1,subQ0]});Q57=makeQuery(id+"F0.imprint","IMPRINT",FACE,{"disambiguationData":[TD([[makeQuery(id+"F0.imprint","IMPRINT",EDGE,{"disambiguationData":[TD([[subQ2,1.0]])],"derivedFrom":subQ1}),1.0]])]});}
            var Q58;
            {var subQ0=sQuery(id+"F0.wireOp",EDGE,"E15.3.0");var subQ1=sQuery(id+"F0.wireOp",EDGE,"E5.0");var subQ2=makeQuery(id+"F0.imprint","INTERSECT",VERTEX,{"derivedFrom":[subQ1,subQ0]});Q58=makeQuery(id+"F0.imprint","IMPRINT",FACE,{"disambiguationData":[TD([[makeQuery(id+"F0.imprint","IMPRINT",EDGE,{"disambiguationData":[TD([[subQ2,-1.0]])],"derivedFrom":subQ1}),1.0]])]});}
            var Q59;
            {var subQ0=sQuery(id+"F0.wireOp",EDGE,"E17.2.0");var subQ1=sQuery(id+"F0.wireOp",EDGE,"E5.0");var subQ2=makeQuery(id+"F0.imprint","INTERSECT",VERTEX,{"disambiguationData":[OD(0.0)],"derivedFrom":[subQ1,subQ0]});Q59=makeQuery(id+"F0.imprint","IMPRINT",FACE,{"disambiguationData":[TD([[makeQuery(id+"F0.imprint","IMPRINT",EDGE,{"disambiguationData":[TD([[subQ2,-1.0]])],"derivedFrom":subQ1}),1.0]])]});}
            var Q60;
            {var subQ0=sQuery(id+"F0.wireOp",EDGE,"E17.2.0");var subQ1=sQuery(id+"F0.wireOp",EDGE,"E5.0");var subQ2=makeQuery(id+"F0.imprint","INTERSECT",VERTEX,{"disambiguationData":[OD(0.0)],"derivedFrom":[subQ1,subQ0]});Q60=makeQuery(id+"F0.imprint","IMPRINT",FACE,{"disambiguationData":[TD([[makeQuery(id+"F0.imprint","IMPRINT",EDGE,{"disambiguationData":[TD([[subQ2,-1.0]])],"derivedFrom":subQ1}),-1.0]])]});}
            var Q61;
            {var subQ0=sQuery(id+"F0.wireOp",EDGE,"E15.1.0");var subQ3=sQuery(id+"F0.wireOp",EDGE,"E4");var subQ4=makeQuery(id+"F0.imprint","INTERSECT",VERTEX,{"derivedFrom":[subQ3,subQ0]});Q61=makeQuery(id+"F0.imprint","IMPRINT",FACE,{"disambiguationData":[TD([[makeQuery(id+"F0.imprint","IMPRINT",EDGE,{"disambiguationData":[TD([[subQ4,-1.0]])],"derivedFrom":subQ3}),-1.0]])]});}
            var Q62;
            {var subQ1=sQuery(id+"F0.wireOp",EDGE,"E4");var subQ5=sQuery(id+"F0.wireOp",EDGE,"E13.0");var subQ8=makeQuery(id+"F0.imprint","INTERSECT",VERTEX,{"derivedFrom":[subQ1,subQ5]});Q62=makeQuery(id+"F0.imprint","IMPRINT",FACE,{"disambiguationData":[TD([[makeQuery(id+"F0.imprint","IMPRINT",EDGE,{"disambiguationData":[TD([[subQ8,-1.0]])],"derivedFrom":subQ1}),-1.0]])]});}
            var Q63;
            {var subQ0=sQuery(id+"F0.wireOp",EDGE,"E5.0");var subQ1=makeQuery(id+"F0.imprint","INTERSECT",VERTEX,{"derivedFrom":[subQ0,sQuery(id+"F0.wireOp",EDGE,"E14.0")]});Q63=makeQuery(id+"F0.imprint","IMPRINT",FACE,{"disambiguationData":[TD([[makeQuery(id+"F0.imprint","IMPRINT",EDGE,{"disambiguationData":[TD([[subQ1,1.0]])],"derivedFrom":subQ0}),-1.0]])]});}
            var Q64;
            {var subQ0=sQuery(id+"F0.wireOp",EDGE,"E14.0");var subQ1=sQuery(id+"F0.wireOp",EDGE,"E5.0");var subQ2=makeQuery(id+"F0.imprint","INTERSECT",VERTEX,{"derivedFrom":[subQ1,subQ0]});Q64=makeQuery(id+"F0.imprint","IMPRINT",FACE,{"disambiguationData":[TD([[makeQuery(id+"F0.imprint","IMPRINT",EDGE,{"disambiguationData":[TD([[subQ2,-1.0]])],"derivedFrom":subQ1}),1.0]])]});}
            var Q65;
            {var subQ0=sQuery(id+"F0.wireOp",EDGE,"E14.0");var subQ1=sQuery(id+"F0.wireOp",EDGE,"E5.0");var subQ2=makeQuery(id+"F0.imprint","INTERSECT",VERTEX,{"derivedFrom":[subQ1,subQ0]});Q65=makeQuery(id+"F0.imprint","IMPRINT",FACE,{"disambiguationData":[TD([[makeQuery(id+"F0.imprint","IMPRINT",EDGE,{"disambiguationData":[TD([[subQ2,1.0]])],"derivedFrom":subQ1}),1.0]])]});}
            var Q66;
            {var subQ3=sQuery(id+"F0.wireOp",EDGE,"E4");var subQ5=sQuery(id+"F0.wireOp",EDGE,"E14.0");var subQ6=makeQuery(id+"F0.imprint","INTERSECT",VERTEX,{"derivedFrom":[subQ3,subQ5]});Q66=makeQuery(id+"F0.imprint","IMPRINT",FACE,{"disambiguationData":[TD([[makeQuery(id+"F0.imprint","IMPRINT",EDGE,{"disambiguationData":[TD([[subQ6,-1.0]])],"derivedFrom":subQ3}),-1.0]])]});}
            var Q67;
            {var subQ0=sQuery(id+"F0.wireOp",EDGE,"E15.17.1");var subQ5=sQuery(id+"F0.wireOp",EDGE,"E4");var subQ6=makeQuery(id+"F0.imprint","INTERSECT",VERTEX,{"derivedFrom":[subQ5,subQ0]});Q67=makeQuery(id+"F0.imprint","IMPRINT",FACE,{"disambiguationData":[TD([[makeQuery(id+"F0.imprint","IMPRINT",EDGE,{"disambiguationData":[TD([[subQ6,1.0]])],"derivedFrom":subQ5}),-1.0]])]});}
            var Q68;
            {var subQ0=sQuery(id+"F0.wireOp",EDGE,"E16");var subQ1=sQuery(id+"F0.wireOp",EDGE,"E5.0");var subQ2=makeQuery(id+"F0.imprint","INTERSECT",VERTEX,{"disambiguationData":[OD(0.0)],"derivedFrom":[subQ1,subQ0]});Q68=makeQuery(id+"F0.imprint","IMPRINT",FACE,{"disambiguationData":[TD([[makeQuery(id+"F0.imprint","IMPRINT",EDGE,{"disambiguationData":[TD([[subQ2,-1.0]])],"derivedFrom":subQ1}),-1.0]])]});}
            var Q69;
            {var subQ0=sQuery(id+"F0.wireOp",EDGE,"E16");var subQ1=sQuery(id+"F0.wireOp",EDGE,"E5.0");var subQ2=makeQuery(id+"F0.imprint","INTERSECT",VERTEX,{"disambiguationData":[OD(0.0)],"derivedFrom":[subQ1,subQ0]});Q69=makeQuery(id+"F0.imprint","IMPRINT",FACE,{"disambiguationData":[TD([[makeQuery(id+"F0.imprint","IMPRINT",EDGE,{"disambiguationData":[TD([[subQ2,-1.0]])],"derivedFrom":subQ1}),1.0]])]});}
            var Q70;
            {var subQ3=sQuery(id+"F0.wireOp",EDGE,"E4");var subQ5=sQuery(id+"F0.wireOp",EDGE,"E15.15.0");var subQ6=makeQuery(id+"F0.imprint","INTERSECT",VERTEX,{"derivedFrom":[subQ3,subQ5]});Q70=makeQuery(id+"F0.imprint","IMPRINT",FACE,{"disambiguationData":[TD([[makeQuery(id+"F0.imprint","IMPRINT",EDGE,{"disambiguationData":[TD([[subQ6,-1.0]])],"derivedFrom":subQ3}),-1.0]])]});}
            var Q71;
            {var subQ0=sQuery(id+"F0.wireOp",EDGE,"E5.0");var subQ1=makeQuery(id+"F0.imprint","INTERSECT",VERTEX,{"derivedFrom":[subQ0,sQuery(id+"F0.wireOp",EDGE,"E15.15.0")]});Q71=makeQuery(id+"F0.imprint","IMPRINT",FACE,{"disambiguationData":[TD([[makeQuery(id+"F0.imprint","IMPRINT",EDGE,{"disambiguationData":[TD([[subQ1,1.0]])],"derivedFrom":subQ0}),-1.0]])]});}
            var Q72;
            {var subQ0=sQuery(id+"F0.wireOp",EDGE,"E15.15.0");var subQ1=sQuery(id+"F0.wireOp",EDGE,"E5.0");var subQ2=makeQuery(id+"F0.imprint","INTERSECT",VERTEX,{"derivedFrom":[subQ1,subQ0]});Q72=makeQuery(id+"F0.imprint","IMPRINT",FACE,{"disambiguationData":[TD([[makeQuery(id+"F0.imprint","IMPRINT",EDGE,{"disambiguationData":[TD([[subQ2,-1.0]])],"derivedFrom":subQ1}),1.0]])]});}
            var Q73;
            {var subQ0=sQuery(id+"F0.wireOp",EDGE,"E15.15.0");var subQ1=sQuery(id+"F0.wireOp",EDGE,"E5.0");var subQ2=makeQuery(id+"F0.imprint","INTERSECT",VERTEX,{"derivedFrom":[subQ1,subQ0]});Q73=makeQuery(id+"F0.imprint","IMPRINT",FACE,{"disambiguationData":[TD([[makeQuery(id+"F0.imprint","IMPRINT",EDGE,{"disambiguationData":[TD([[subQ2,1.0]])],"derivedFrom":subQ1}),1.0]])]});}
            var Q74;
            {var subQ0=sQuery(id+"F0.wireOp",EDGE,"E15.15.1");var subQ3=sQuery(id+"F0.wireOp",EDGE,"E4");var subQ4=makeQuery(id+"F0.imprint","INTERSECT",VERTEX,{"derivedFrom":[subQ3,subQ0]});Q74=makeQuery(id+"F0.imprint","IMPRINT",FACE,{"disambiguationData":[TD([[makeQuery(id+"F0.imprint","IMPRINT",EDGE,{"disambiguationData":[TD([[subQ4,-1.0]])],"derivedFrom":subQ3}),-1.0]])]});}
            var Q75;
            {var subQ0=sQuery(id+"F0.wireOp",EDGE,"E15.13.0");var subQ3=sQuery(id+"F0.wireOp",EDGE,"E4");var subQ4=makeQuery(id+"F0.imprint","INTERSECT",VERTEX,{"derivedFrom":[subQ3,subQ0]});Q75=makeQuery(id+"F0.imprint","IMPRINT",FACE,{"disambiguationData":[TD([[makeQuery(id+"F0.imprint","IMPRINT",EDGE,{"disambiguationData":[TD([[subQ4,-1.0]])],"derivedFrom":subQ3}),-1.0]])]});}
            var Q76;
            {var subQ0=sQuery(id+"F0.wireOp",EDGE,"E17.10.0");var subQ1=sQuery(id+"F0.wireOp",EDGE,"E5.0");var subQ2=makeQuery(id+"F0.imprint","INTERSECT",VERTEX,{"disambiguationData":[OD(0.0)],"derivedFrom":[subQ1,subQ0]});Q76=makeQuery(id+"F0.imprint","IMPRINT",FACE,{"disambiguationData":[TD([[makeQuery(id+"F0.imprint","IMPRINT",EDGE,{"disambiguationData":[TD([[subQ2,-1.0]])],"derivedFrom":subQ1}),-1.0]])]});}
            var Q77;
            {var subQ0=sQuery(id+"F0.wireOp",EDGE,"E17.10.0");var subQ1=sQuery(id+"F0.wireOp",EDGE,"E5.0");var subQ2=makeQuery(id+"F0.imprint","INTERSECT",VERTEX,{"disambiguationData":[OD(0.0)],"derivedFrom":[subQ1,subQ0]});Q77=makeQuery(id+"F0.imprint","IMPRINT",FACE,{"disambiguationData":[TD([[makeQuery(id+"F0.imprint","IMPRINT",EDGE,{"disambiguationData":[TD([[subQ2,-1.0]])],"derivedFrom":subQ1}),1.0]])]});}
            var Q78;
            {var subQ3=sQuery(id+"F0.wireOp",EDGE,"E4");var subQ5=sQuery(id+"F0.wireOp",EDGE,"E15.12.0");var subQ6=makeQuery(id+"F0.imprint","INTERSECT",VERTEX,{"derivedFrom":[subQ3,subQ5]});Q78=makeQuery(id+"F0.imprint","IMPRINT",FACE,{"disambiguationData":[TD([[makeQuery(id+"F0.imprint","IMPRINT",EDGE,{"disambiguationData":[TD([[subQ6,-1.0]])],"derivedFrom":subQ3}),-1.0]])]});}
            var Q79;
            {var subQ1=sQuery(id+"F0.wireOp",EDGE,"E4");var subQ5=sQuery(id+"F0.wireOp",EDGE,"E15.12.1");var subQ9=makeQuery(id+"F0.imprint","INTERSECT",VERTEX,{"derivedFrom":[subQ1,subQ5]});Q79=makeQuery(id+"F0.imprint","IMPRINT",FACE,{"disambiguationData":[TD([[makeQuery(id+"F0.imprint","IMPRINT",EDGE,{"disambiguationData":[TD([[subQ9,-1.0]])],"derivedFrom":subQ1}),-1.0]])]});}
            var Q80;
            {var subQ0=sQuery(id+"F0.wireOp",EDGE,"E15.12.0");var subQ1=sQuery(id+"F0.wireOp",EDGE,"E5.0");var subQ2=makeQuery(id+"F0.imprint","INTERSECT",VERTEX,{"derivedFrom":[subQ1,subQ0]});Q80=makeQuery(id+"F0.imprint","IMPRINT",FACE,{"disambiguationData":[TD([[makeQuery(id+"F0.imprint","IMPRINT",EDGE,{"disambiguationData":[TD([[subQ2,1.0]])],"derivedFrom":subQ1}),1.0]])]});}
            var Q81;
            {var subQ0=sQuery(id+"F0.wireOp",EDGE,"E15.12.0");var subQ1=sQuery(id+"F0.wireOp",EDGE,"E5.0");var subQ2=makeQuery(id+"F0.imprint","INTERSECT",VERTEX,{"derivedFrom":[subQ1,subQ0]});Q81=makeQuery(id+"F0.imprint","IMPRINT",FACE,{"disambiguationData":[TD([[makeQuery(id+"F0.imprint","IMPRINT",EDGE,{"disambiguationData":[TD([[subQ2,-1.0]])],"derivedFrom":subQ1}),1.0]])]});}
            var Q82;
            {var subQ0=sQuery(id+"F0.wireOp",EDGE,"E15.10.0");var subQ3=sQuery(id+"F0.wireOp",EDGE,"E4");var subQ4=makeQuery(id+"F0.imprint","INTERSECT",VERTEX,{"derivedFrom":[subQ3,subQ0]});Q82=makeQuery(id+"F0.imprint","IMPRINT",FACE,{"disambiguationData":[TD([[makeQuery(id+"F0.imprint","IMPRINT",EDGE,{"disambiguationData":[TD([[subQ4,-1.0]])],"derivedFrom":subQ3}),-1.0]])]});}
            var Q83;
            {var subQ0=sQuery(id+"F0.wireOp",EDGE,"E17.8.0");var subQ1=sQuery(id+"F0.wireOp",EDGE,"E5.0");var subQ2=makeQuery(id+"F0.imprint","INTERSECT",VERTEX,{"disambiguationData":[OD(0.0)],"derivedFrom":[subQ1,subQ0]});Q83=makeQuery(id+"F0.imprint","IMPRINT",FACE,{"disambiguationData":[TD([[makeQuery(id+"F0.imprint","IMPRINT",EDGE,{"disambiguationData":[TD([[subQ2,-1.0]])],"derivedFrom":subQ1}),1.0]])]});}
            var Q84;
            {var subQ0=sQuery(id+"F0.wireOp",EDGE,"E17.8.0");var subQ1=sQuery(id+"F0.wireOp",EDGE,"E5.0");var subQ2=makeQuery(id+"F0.imprint","INTERSECT",VERTEX,{"disambiguationData":[OD(0.0)],"derivedFrom":[subQ1,subQ0]});Q84=makeQuery(id+"F0.imprint","IMPRINT",FACE,{"disambiguationData":[TD([[makeQuery(id+"F0.imprint","IMPRINT",EDGE,{"disambiguationData":[TD([[subQ2,-1.0]])],"derivedFrom":subQ1}),-1.0]])]});}
            var Q85;
            {var subQ3=sQuery(id+"F0.wireOp",EDGE,"E4");var subQ5=sQuery(id+"F0.wireOp",EDGE,"E15.9.0");var subQ6=makeQuery(id+"F0.imprint","INTERSECT",VERTEX,{"derivedFrom":[subQ3,subQ5]});Q85=makeQuery(id+"F0.imprint","IMPRINT",FACE,{"disambiguationData":[TD([[makeQuery(id+"F0.imprint","IMPRINT",EDGE,{"disambiguationData":[TD([[subQ6,-1.0]])],"derivedFrom":subQ3}),-1.0]])]});}
            var Q86;
            {var subQ0=sQuery(id+"F0.wireOp",EDGE,"E15.9.1");var subQ3=sQuery(id+"F0.wireOp",EDGE,"E4");var subQ4=makeQuery(id+"F0.imprint","INTERSECT",VERTEX,{"derivedFrom":[subQ3,subQ0]});Q86=makeQuery(id+"F0.imprint","IMPRINT",FACE,{"disambiguationData":[TD([[makeQuery(id+"F0.imprint","IMPRINT",EDGE,{"disambiguationData":[TD([[subQ4,-1.0]])],"derivedFrom":subQ3}),-1.0]])]});}
            var Q87;
            {var subQ0=sQuery(id+"F0.wireOp",EDGE,"E15.9.0");var subQ1=sQuery(id+"F0.wireOp",EDGE,"E5.0");var subQ2=makeQuery(id+"F0.imprint","INTERSECT",VERTEX,{"derivedFrom":[subQ1,subQ0]});Q87=makeQuery(id+"F0.imprint","IMPRINT",FACE,{"disambiguationData":[TD([[makeQuery(id+"F0.imprint","IMPRINT",EDGE,{"disambiguationData":[TD([[subQ2,1.0]])],"derivedFrom":subQ1}),1.0]])]});}
            var Q88;
            {var subQ0=sQuery(id+"F0.wireOp",EDGE,"E15.9.0");var subQ1=sQuery(id+"F0.wireOp",EDGE,"E5.0");var subQ2=makeQuery(id+"F0.imprint","INTERSECT",VERTEX,{"derivedFrom":[subQ1,subQ0]});Q88=makeQuery(id+"F0.imprint","IMPRINT",FACE,{"disambiguationData":[TD([[makeQuery(id+"F0.imprint","IMPRINT",EDGE,{"disambiguationData":[TD([[subQ2,-1.0]])],"derivedFrom":subQ1}),1.0]])]});}
            var Q89;
            {var subQ0=sQuery(id+"F0.wireOp",EDGE,"E5.0");var subQ1=makeQuery(id+"F0.imprint","INTERSECT",VERTEX,{"derivedFrom":[subQ0,sQuery(id+"F0.wireOp",EDGE,"E15.9.0")]});Q89=makeQuery(id+"F0.imprint","IMPRINT",FACE,{"disambiguationData":[TD([[makeQuery(id+"F0.imprint","IMPRINT",EDGE,{"disambiguationData":[TD([[subQ1,1.0]])],"derivedFrom":subQ0}),-1.0]])]});}
            var Q90;
            {var subQ0=sQuery(id+"F0.wireOp",EDGE,"E15.7.0");var subQ3=sQuery(id+"F0.wireOp",EDGE,"E4");var subQ4=makeQuery(id+"F0.imprint","INTERSECT",VERTEX,{"derivedFrom":[subQ3,subQ0]});Q90=makeQuery(id+"F0.imprint","IMPRINT",FACE,{"disambiguationData":[TD([[makeQuery(id+"F0.imprint","IMPRINT",EDGE,{"disambiguationData":[TD([[subQ4,-1.0]])],"derivedFrom":subQ3}),-1.0]])]});}
            var Q91;
            {var subQ0=sQuery(id+"F0.wireOp",EDGE,"E17.6.0");var subQ1=sQuery(id+"F0.wireOp",EDGE,"E5.0");var subQ2=makeQuery(id+"F0.imprint","INTERSECT",VERTEX,{"disambiguationData":[OD(0.0)],"derivedFrom":[subQ1,subQ0]});Q91=makeQuery(id+"F0.imprint","IMPRINT",FACE,{"disambiguationData":[TD([[makeQuery(id+"F0.imprint","IMPRINT",EDGE,{"disambiguationData":[TD([[subQ2,-1.0]])],"derivedFrom":subQ1}),1.0]])]});}
            var Q92;
            {var subQ0=sQuery(id+"F0.wireOp",EDGE,"E17.6.0");var subQ1=sQuery(id+"F0.wireOp",EDGE,"E5.0");var subQ2=makeQuery(id+"F0.imprint","INTERSECT",VERTEX,{"disambiguationData":[OD(0.0)],"derivedFrom":[subQ1,subQ0]});Q92=makeQuery(id+"F0.imprint","IMPRINT",FACE,{"disambiguationData":[TD([[makeQuery(id+"F0.imprint","IMPRINT",EDGE,{"disambiguationData":[TD([[subQ2,-1.0]])],"derivedFrom":subQ1}),-1.0]])]});}
            var Q93;
            Q93=makeQuery(id+"F0.imprint","IMPRINT",FACE,{"disambiguationData":[TD([[makeQuery(id+"F0.imprint","IMPRINT",EDGE,{"derivedFrom":sQuery(id+"F0.wireOp",EDGE,"E0")}),-1.0]])]});
            var Q94;
            {var subQ0=sQuery(id+"F0.wireOp",EDGE,"E5.0");var subQ1=makeQuery(id+"F0.imprint","INTERSECT",VERTEX,{"derivedFrom":[subQ0,sQuery(id+"F0.wireOp",EDGE,"E15.12.0")]});Q94=makeQuery(id+"F0.imprint","IMPRINT",FACE,{"disambiguationData":[TD([[makeQuery(id+"F0.imprint","IMPRINT",EDGE,{"disambiguationData":[TD([[subQ1,1.0]])],"derivedFrom":subQ0}),-1.0]])]});}
            extrude(context, id + "F1", {"entities" : qUnion([Q0, Q1, Q2, Q3, Q4, Q5, Q6, Q7, Q8, Q9, Q10, Q11, Q12, Q13, Q14, Q15, Q16, Q17, Q18, Q19, Q20, Q21, Q22, Q23, Q24, Q25, Q26, Q27, Q28, Q29, Q30, Q31, Q32, Q33, Q34, Q35, Q36, Q37, Q38, Q39, Q40, Q41, Q42, Q43, Q44, Q45, Q46, Q47, Q48, Q49, Q50, Q51, Q52, Q53, Q54, Q55, Q56, Q57, Q58, Q59, Q60, Q61, Q62, Q63, Q64, Q65, Q66, Q67, Q68, Q69, Q70, Q71, Q72, Q73, Q74, Q75, Q76, Q77, Q78, Q79, Q80, Q81, Q82, Q83, Q84, Q85, Q86, Q87, Q88, Q89, Q90, Q91, Q92, Q93, Q94]), "depth" : 25 * mm});
        }
        {
            var Q0;
            Q0=makeQuery(id+"F0.imprint","IMPRINT",FACE,{"disambiguationData":[TD([[makeQuery(id+"F0.imprint","IMPRINT",EDGE,{"derivedFrom":sQuery(id+"F0.wireOp",EDGE,"E6")}),1.0]])]});
            var Q1;
            {var subQ0=sQuery(id+"F0.wireOp",EDGE,"E15.4.1");var subQ1=sQuery(id+"F0.wireOp",EDGE,"E4");var subQ2=makeQuery(id+"F0.imprint","INTERSECT",VERTEX,{"derivedFrom":[subQ1,subQ0]});Q1=makeQuery(id+"F0.imprint","IMPRINT",FACE,{"disambiguationData":[TD([[makeQuery(id+"F0.imprint","IMPRINT",EDGE,{"disambiguationData":[TD([[subQ2,-1.0]])],"derivedFrom":subQ1}),-1.0]])]});}
            var Q2;
            {var subQ0=sQuery(id+"F0.wireOp",EDGE,"E15.5.0");var subQ1=sQuery(id+"F0.wireOp",EDGE,"E4");var subQ2=makeQuery(id+"F0.imprint","INTERSECT",VERTEX,{"derivedFrom":[subQ1,subQ0]});Q2=makeQuery(id+"F0.imprint","IMPRINT",FACE,{"disambiguationData":[TD([[makeQuery(id+"F0.imprint","IMPRINT",EDGE,{"disambiguationData":[TD([[subQ2,-1.0]])],"derivedFrom":subQ1}),-1.0]])]});}
            var Q3;
            {var subQ0=sQuery(id+"F0.wireOp",EDGE,"E15.5.1");var subQ1=sQuery(id+"F0.wireOp",EDGE,"E4");var subQ2=makeQuery(id+"F0.imprint","INTERSECT",VERTEX,{"derivedFrom":[subQ1,subQ0]});Q3=makeQuery(id+"F0.imprint","IMPRINT",FACE,{"disambiguationData":[TD([[makeQuery(id+"F0.imprint","IMPRINT",EDGE,{"disambiguationData":[TD([[subQ2,-1.0]])],"derivedFrom":subQ1}),-1.0]])]});}
            var Q4;
            {var subQ0=sQuery(id+"F0.wireOp",EDGE,"E15.6.1");var subQ3=sQuery(id+"F0.wireOp",EDGE,"E4");var subQ4=makeQuery(id+"F0.imprint","INTERSECT",VERTEX,{"derivedFrom":[subQ3,subQ0]});Q4=makeQuery(id+"F0.imprint","IMPRINT",FACE,{"disambiguationData":[TD([[makeQuery(id+"F0.imprint","IMPRINT",EDGE,{"disambiguationData":[TD([[subQ4,-1.0]])],"derivedFrom":subQ3}),-1.0]])]});}
            var Q5;
            {var subQ0=sQuery(id+"F0.wireOp",EDGE,"E15.6.1");var subQ1=makeQuery(id+"F0.imprint","IMPRINT",VERTEX,{"derivedFrom":subQ0});Q5=makeQuery(id+"F0.imprint","IMPRINT",FACE,{"disambiguationData":[TD([[makeQuery(id+"F0.imprint","IMPRINT",EDGE,{"disambiguationData":[TD([[subQ1,1.0]])],"derivedFrom":subQ0}),-1.0]])]});}
            var Q6;
            {var subQ0=sQuery(id+"F0.wireOp",EDGE,"E15.4.0");var subQ1=makeQuery(id+"F0.imprint","IMPRINT",VERTEX,{"derivedFrom":subQ0});Q6=makeQuery(id+"F0.imprint","IMPRINT",FACE,{"disambiguationData":[TD([[makeQuery(id+"F0.imprint","IMPRINT",EDGE,{"disambiguationData":[TD([[subQ1,1.0]])],"derivedFrom":subQ0}),1.0]])]});}
            var Q7;
            {var subQ5=sQuery(id+"F0.wireOp",EDGE,"E15.4.1");var subQ7=makeQuery(id+"F0.imprint","IMPRINT",VERTEX,{"derivedFrom":subQ5});Q7=makeQuery(id+"F0.imprint","IMPRINT",FACE,{"disambiguationData":[TD([[makeQuery(id+"F0.imprint","IMPRINT",EDGE,{"disambiguationData":[TD([[subQ7,1.0]])],"derivedFrom":subQ5}),-1.0]])]});}
            var Q8;
            {var subQ0=sQuery(id+"F0.wireOp",EDGE,"E15.4.0");var subQ1=makeQuery(id+"F0.imprint","IMPRINT",VERTEX,{"derivedFrom":subQ0});Q8=makeQuery(id+"F0.imprint","IMPRINT",FACE,{"disambiguationData":[TD([[makeQuery(id+"F0.imprint","IMPRINT",EDGE,{"disambiguationData":[TD([[subQ1,1.0]])],"derivedFrom":subQ0}),-1.0]])]});}
            var Q9;
            {var subQ0=sQuery(id+"F0.wireOp",EDGE,"E15.2.0");var subQ1=sQuery(id+"F0.wireOp",EDGE,"E4");var subQ2=makeQuery(id+"F0.imprint","INTERSECT",VERTEX,{"derivedFrom":[subQ1,subQ0]});Q9=makeQuery(id+"F0.imprint","IMPRINT",FACE,{"disambiguationData":[TD([[makeQuery(id+"F0.imprint","IMPRINT",EDGE,{"disambiguationData":[TD([[subQ2,-1.0]])],"derivedFrom":subQ1}),-1.0]])]});}
            var Q10;
            {var subQ0=sQuery(id+"F0.wireOp",EDGE,"E15.3.1");var subQ1=sQuery(id+"F0.wireOp",EDGE,"E3.0");var subQ2=makeQuery(id+"F0.imprint","INTERSECT",VERTEX,{"derivedFrom":[subQ1,subQ0]});Q10=makeQuery(id+"F0.imprint","IMPRINT",FACE,{"disambiguationData":[TD([[makeQuery(id+"F0.imprint","IMPRINT",EDGE,{"disambiguationData":[TD([[subQ2,-1.0]])],"derivedFrom":subQ1}),-1.0]])]});}
            var Q11;
            {var subQ0=sQuery(id+"F0.wireOp",EDGE,"E15.2.0");var subQ1=makeQuery(id+"F0.imprint","IMPRINT",VERTEX,{"derivedFrom":subQ0});Q11=makeQuery(id+"F0.imprint","IMPRINT",FACE,{"disambiguationData":[TD([[makeQuery(id+"F0.imprint","IMPRINT",EDGE,{"disambiguationData":[TD([[subQ1,1.0]])],"derivedFrom":subQ0}),1.0]])]});}
            var Q12;
            {var subQ0=sQuery(id+"F0.wireOp",EDGE,"E10.2.0");var subQ1=sQuery(id+"F0.wireOp",EDGE,"E1.0");var subQ2=makeQuery(id+"F0.imprint","INTERSECT",VERTEX,{"derivedFrom":[subQ1,subQ0]});Q12=makeQuery(id+"F0.imprint","IMPRINT",FACE,{"disambiguationData":[TD([[makeQuery(id+"F0.imprint","IMPRINT",EDGE,{"disambiguationData":[TD([[subQ2,-1.0]])],"derivedFrom":subQ1}),-1.0]])]});}
            var Q13;
            {var subQ0=sQuery(id+"F0.wireOp",EDGE,"E10.3.0");var subQ1=sQuery(id+"F0.wireOp",EDGE,"E1.0");var subQ2=makeQuery(id+"F0.imprint","INTERSECT",VERTEX,{"derivedFrom":[subQ1,subQ0]});Q13=makeQuery(id+"F0.imprint","IMPRINT",FACE,{"disambiguationData":[TD([[makeQuery(id+"F0.imprint","IMPRINT",EDGE,{"disambiguationData":[TD([[subQ2,-1.0]])],"derivedFrom":subQ1}),-1.0]])]});}
            var Q14;
            {var subQ0=sQuery(id+"F0.wireOp",EDGE,"E10.4.0");var subQ1=sQuery(id+"F0.wireOp",EDGE,"E1.0");var subQ2=makeQuery(id+"F0.imprint","INTERSECT",VERTEX,{"derivedFrom":[subQ1,subQ0]});Q14=makeQuery(id+"F0.imprint","IMPRINT",FACE,{"disambiguationData":[TD([[makeQuery(id+"F0.imprint","IMPRINT",EDGE,{"disambiguationData":[TD([[subQ2,-1.0]])],"derivedFrom":subQ1}),-1.0]])]});}
            var Q15;
            {var subQ0=sQuery(id+"F0.wireOp",EDGE,"E10.5.0");var subQ1=sQuery(id+"F0.wireOp",EDGE,"E1.0");var subQ2=makeQuery(id+"F0.imprint","INTERSECT",VERTEX,{"derivedFrom":[subQ1,subQ0]});Q15=makeQuery(id+"F0.imprint","IMPRINT",FACE,{"disambiguationData":[TD([[makeQuery(id+"F0.imprint","IMPRINT",EDGE,{"disambiguationData":[TD([[subQ2,-1.0]])],"derivedFrom":subQ1}),-1.0]])]});}
            var Q16;
            {var subQ0=sQuery(id+"F0.wireOp",EDGE,"E10.7.0");var subQ1=sQuery(id+"F0.wireOp",EDGE,"E1.0");var subQ2=makeQuery(id+"F0.imprint","INTERSECT",VERTEX,{"derivedFrom":[subQ1,subQ0]});Q16=makeQuery(id+"F0.imprint","IMPRINT",FACE,{"disambiguationData":[TD([[makeQuery(id+"F0.imprint","IMPRINT",EDGE,{"disambiguationData":[TD([[subQ2,-1.0]])],"derivedFrom":subQ1}),-1.0]])]});}
            var Q17;
            {var subQ0=sQuery(id+"F0.wireOp",EDGE,"E10.8.0");var subQ1=sQuery(id+"F0.wireOp",EDGE,"E1.0");var subQ2=makeQuery(id+"F0.imprint","INTERSECT",VERTEX,{"derivedFrom":[subQ1,subQ0]});Q17=makeQuery(id+"F0.imprint","IMPRINT",FACE,{"disambiguationData":[TD([[makeQuery(id+"F0.imprint","IMPRINT",EDGE,{"disambiguationData":[TD([[subQ2,-1.0]])],"derivedFrom":subQ1}),-1.0]])]});}
            var Q18;
            {var subQ0=sQuery(id+"F0.wireOp",EDGE,"E10.1.2");var subQ1=sQuery(id+"F0.wireOp",EDGE,"E1.0");var subQ2=makeQuery(id+"F0.imprint","INTERSECT",VERTEX,{"derivedFrom":[subQ1,subQ0]});Q18=makeQuery(id+"F0.imprint","IMPRINT",FACE,{"disambiguationData":[TD([[makeQuery(id+"F0.imprint","IMPRINT",EDGE,{"disambiguationData":[TD([[subQ2,1.0]])],"derivedFrom":subQ1}),-1.0]])]});}
            var Q19;
            {var subQ0=sQuery(id+"F0.wireOp",EDGE,"E10.1.0");var subQ1=sQuery(id+"F0.wireOp",EDGE,"E1.0");var subQ2=makeQuery(id+"F0.imprint","INTERSECT",VERTEX,{"derivedFrom":[subQ1,subQ0]});Q19=makeQuery(id+"F0.imprint","IMPRINT",FACE,{"disambiguationData":[TD([[makeQuery(id+"F0.imprint","IMPRINT",EDGE,{"disambiguationData":[TD([[subQ2,-1.0]])],"derivedFrom":subQ1}),-1.0]])]});}
            var Q20;
            {var subQ0=sQuery(id+"F0.wireOp",EDGE,"E15.2.1");var subQ1=makeQuery(id+"F0.imprint","IMPRINT",VERTEX,{"derivedFrom":subQ0});Q20=makeQuery(id+"F0.imprint","IMPRINT",FACE,{"disambiguationData":[TD([[makeQuery(id+"F0.imprint","IMPRINT",EDGE,{"disambiguationData":[TD([[subQ1,1.0]])],"derivedFrom":subQ0}),-1.0]])]});}
            var Q21;
            {var subQ0=sQuery(id+"F0.wireOp",EDGE,"E14.0");var subQ1=makeQuery(id+"F0.imprint","IMPRINT",VERTEX,{"derivedFrom":subQ0});Q21=makeQuery(id+"F0.imprint","IMPRINT",FACE,{"disambiguationData":[TD([[makeQuery(id+"F0.imprint","IMPRINT",EDGE,{"disambiguationData":[TD([[subQ1,1.0]])],"derivedFrom":subQ0}),1.0]])]});}
            var Q22;
            {var subQ0=sQuery(id+"F0.wireOp",EDGE,"E13.0");var subQ1=makeQuery(id+"F0.imprint","IMPRINT",VERTEX,{"derivedFrom":subQ0});Q22=makeQuery(id+"F0.imprint","IMPRINT",FACE,{"disambiguationData":[TD([[makeQuery(id+"F0.imprint","IMPRINT",EDGE,{"disambiguationData":[TD([[subQ1,1.0]])],"derivedFrom":subQ0}),-1.0]])]});}
            var Q23;
            {var subQ0=sQuery(id+"F0.wireOp",EDGE,"E15.16.0");var subQ1=makeQuery(id+"F0.imprint","IMPRINT",VERTEX,{"derivedFrom":subQ0});Q23=makeQuery(id+"F0.imprint","IMPRINT",FACE,{"disambiguationData":[TD([[makeQuery(id+"F0.imprint","IMPRINT",EDGE,{"disambiguationData":[TD([[subQ1,1.0]])],"derivedFrom":subQ0}),1.0]])]});}
            var Q24;
            {var subQ0=sQuery(id+"F0.wireOp",EDGE,"E15.16.1");var subQ1=makeQuery(id+"F0.imprint","IMPRINT",VERTEX,{"derivedFrom":subQ0});Q24=makeQuery(id+"F0.imprint","IMPRINT",FACE,{"disambiguationData":[TD([[makeQuery(id+"F0.imprint","IMPRINT",EDGE,{"disambiguationData":[TD([[subQ1,1.0]])],"derivedFrom":subQ0}),-1.0]])]});}
            var Q25;
            {var subQ0=sQuery(id+"F0.wireOp",EDGE,"E15.14.1");var subQ1=makeQuery(id+"F0.imprint","IMPRINT",VERTEX,{"derivedFrom":subQ0});Q25=makeQuery(id+"F0.imprint","IMPRINT",FACE,{"disambiguationData":[TD([[makeQuery(id+"F0.imprint","IMPRINT",EDGE,{"disambiguationData":[TD([[subQ1,1.0]])],"derivedFrom":subQ0}),-1.0]])]});}
            var Q26;
            {var subQ0=sQuery(id+"F0.wireOp",EDGE,"E15.12.0");var subQ1=makeQuery(id+"F0.imprint","IMPRINT",VERTEX,{"derivedFrom":subQ0});Q26=makeQuery(id+"F0.imprint","IMPRINT",FACE,{"disambiguationData":[TD([[makeQuery(id+"F0.imprint","IMPRINT",EDGE,{"disambiguationData":[TD([[subQ1,1.0]])],"derivedFrom":subQ0}),1.0]])]});}
            var Q27;
            {var subQ0=sQuery(id+"F0.wireOp",EDGE,"E15.12.1");var subQ1=makeQuery(id+"F0.imprint","IMPRINT",VERTEX,{"derivedFrom":subQ0});Q27=makeQuery(id+"F0.imprint","IMPRINT",FACE,{"disambiguationData":[TD([[makeQuery(id+"F0.imprint","IMPRINT",EDGE,{"disambiguationData":[TD([[subQ1,1.0]])],"derivedFrom":subQ0}),-1.0]])]});}
            var Q28;
            {var subQ0=sQuery(id+"F0.wireOp",EDGE,"E15.10.0");var subQ1=makeQuery(id+"F0.imprint","IMPRINT",VERTEX,{"derivedFrom":subQ0});Q28=makeQuery(id+"F0.imprint","IMPRINT",FACE,{"disambiguationData":[TD([[makeQuery(id+"F0.imprint","IMPRINT",EDGE,{"disambiguationData":[TD([[subQ1,1.0]])],"derivedFrom":subQ0}),1.0]])]});}
            var Q29;
            {var subQ0=sQuery(id+"F0.wireOp",EDGE,"E15.10.1");var subQ1=makeQuery(id+"F0.imprint","IMPRINT",VERTEX,{"derivedFrom":subQ0});Q29=makeQuery(id+"F0.imprint","IMPRINT",FACE,{"disambiguationData":[TD([[makeQuery(id+"F0.imprint","IMPRINT",EDGE,{"disambiguationData":[TD([[subQ1,1.0]])],"derivedFrom":subQ0}),-1.0]])]});}
            var Q30;
            {var subQ0=sQuery(id+"F0.wireOp",EDGE,"E15.8.0");var subQ7=makeQuery(id+"F0.imprint","IMPRINT",VERTEX,{"derivedFrom":subQ0});Q30=makeQuery(id+"F0.imprint","IMPRINT",FACE,{"disambiguationData":[TD([[makeQuery(id+"F0.imprint","IMPRINT",EDGE,{"disambiguationData":[TD([[subQ7,1.0]])],"derivedFrom":subQ0}),1.0]])]});}
            var Q31;
            {var subQ5=sQuery(id+"F0.wireOp",EDGE,"E15.8.1");var subQ7=makeQuery(id+"F0.imprint","IMPRINT",VERTEX,{"derivedFrom":subQ5});Q31=makeQuery(id+"F0.imprint","IMPRINT",FACE,{"disambiguationData":[TD([[makeQuery(id+"F0.imprint","IMPRINT",EDGE,{"disambiguationData":[TD([[subQ7,1.0]])],"derivedFrom":subQ5}),-1.0]])]});}
            var Q32;
            {var subQ0=sQuery(id+"F0.wireOp",EDGE,"E15.6.0");var subQ5=makeQuery(id+"F0.imprint","IMPRINT",VERTEX,{"derivedFrom":subQ0});Q32=makeQuery(id+"F0.imprint","IMPRINT",FACE,{"disambiguationData":[TD([[makeQuery(id+"F0.imprint","IMPRINT",EDGE,{"disambiguationData":[TD([[subQ5,1.0]])],"derivedFrom":subQ0}),1.0]])]});}
            var Q33;
            {var subQ0=sQuery(id+"F0.wireOp",EDGE,"E15.6.0");var subQ1=sQuery(id+"F0.wireOp",EDGE,"E4");var subQ2=makeQuery(id+"F0.imprint","INTERSECT",VERTEX,{"derivedFrom":[subQ1,subQ0]});Q33=makeQuery(id+"F0.imprint","IMPRINT",FACE,{"disambiguationData":[TD([[makeQuery(id+"F0.imprint","IMPRINT",EDGE,{"disambiguationData":[TD([[subQ2,-1.0]])],"derivedFrom":subQ1}),-1.0]])]});}
            var Q34;
            {var subQ0=sQuery(id+"F0.wireOp",EDGE,"E15.7.1");var subQ1=sQuery(id+"F0.wireOp",EDGE,"E4");var subQ2=makeQuery(id+"F0.imprint","INTERSECT",VERTEX,{"derivedFrom":[subQ1,subQ0]});Q34=makeQuery(id+"F0.imprint","IMPRINT",FACE,{"disambiguationData":[TD([[makeQuery(id+"F0.imprint","IMPRINT",EDGE,{"disambiguationData":[TD([[subQ2,-1.0]])],"derivedFrom":subQ1}),-1.0]])]});}
            var Q35;
            {var subQ0=sQuery(id+"F0.wireOp",EDGE,"E15.7.1");var subQ1=sQuery(id+"F0.wireOp",EDGE,"E3.0");var subQ2=makeQuery(id+"F0.imprint","INTERSECT",VERTEX,{"derivedFrom":[subQ1,subQ0]});Q35=makeQuery(id+"F0.imprint","IMPRINT",FACE,{"disambiguationData":[TD([[makeQuery(id+"F0.imprint","IMPRINT",EDGE,{"disambiguationData":[TD([[subQ2,-1.0]])],"derivedFrom":subQ1}),-1.0]])]});}
            var Q36;
            {var subQ0=sQuery(id+"F0.wireOp",EDGE,"E15.6.0");var subQ1=makeQuery(id+"F0.imprint","IMPRINT",VERTEX,{"derivedFrom":subQ0});Q36=makeQuery(id+"F0.imprint","IMPRINT",FACE,{"disambiguationData":[TD([[makeQuery(id+"F0.imprint","IMPRINT",EDGE,{"disambiguationData":[TD([[subQ1,1.0]])],"derivedFrom":subQ0}),-1.0]])]});}
            var Q37;
            {var subQ7=sQuery(id+"F0.wireOp",EDGE,"E10.4.0");var subQ8=sQuery(id+"F0.wireOp",EDGE,"E2");var subQ9=makeQuery(id+"F0.imprint","INTERSECT",VERTEX,{"derivedFrom":[subQ8,subQ7]});Q37=makeQuery(id+"F0.imprint","IMPRINT",FACE,{"disambiguationData":[TD([[makeQuery(id+"F0.imprint","IMPRINT",EDGE,{"disambiguationData":[TD([[subQ9,-1.0]])],"derivedFrom":subQ8}),-1.0]])]});}
            var Q38;
            {var subQ1=sQuery(id+"F0.wireOp",EDGE,"E10.4.2");var subQ3=sQuery(id+"F0.wireOp",EDGE,"E2");var subQ4=makeQuery(id+"F0.imprint","INTERSECT",VERTEX,{"derivedFrom":[subQ3,subQ1]});Q38=makeQuery(id+"F0.imprint","IMPRINT",FACE,{"disambiguationData":[TD([[makeQuery(id+"F0.imprint","IMPRINT",EDGE,{"disambiguationData":[TD([[subQ4,-1.0]])],"derivedFrom":subQ3}),-1.0]])]});}
            var Q39;
            {var subQ0=sQuery(id+"F0.wireOp",EDGE,"E10.4.2");var subQ1=sQuery(id+"F0.wireOp",EDGE,"E1.0");var subQ2=makeQuery(id+"F0.imprint","INTERSECT",VERTEX,{"derivedFrom":[subQ1,subQ0]});Q39=makeQuery(id+"F0.imprint","IMPRINT",FACE,{"disambiguationData":[TD([[makeQuery(id+"F0.imprint","IMPRINT",EDGE,{"disambiguationData":[TD([[subQ2,-1.0]])],"derivedFrom":subQ1}),-1.0]])]});}
            var Q40;
            {var subQ0=sQuery(id+"F0.wireOp",EDGE,"E15.7.0");var subQ3=sQuery(id+"F0.wireOp",EDGE,"E4");var subQ4=makeQuery(id+"F0.imprint","INTERSECT",VERTEX,{"derivedFrom":[subQ3,subQ0]});Q40=makeQuery(id+"F0.imprint","IMPRINT",FACE,{"disambiguationData":[TD([[makeQuery(id+"F0.imprint","IMPRINT",EDGE,{"disambiguationData":[TD([[subQ4,-1.0]])],"derivedFrom":subQ3}),-1.0]])]});}
            var Q41;
            {var subQ0=sQuery(id+"F0.wireOp",EDGE,"E15.8.1");var subQ1=sQuery(id+"F0.wireOp",EDGE,"E4");var subQ2=makeQuery(id+"F0.imprint","INTERSECT",VERTEX,{"derivedFrom":[subQ1,subQ0]});Q41=makeQuery(id+"F0.imprint","IMPRINT",FACE,{"disambiguationData":[TD([[makeQuery(id+"F0.imprint","IMPRINT",EDGE,{"disambiguationData":[TD([[subQ2,-1.0]])],"derivedFrom":subQ1}),-1.0]])]});}
            var Q42;
            {var subQ0=sQuery(id+"F0.wireOp",EDGE,"E10.6.0");var subQ1=sQuery(id+"F0.wireOp",EDGE,"E1.0");var subQ2=makeQuery(id+"F0.imprint","INTERSECT",VERTEX,{"derivedFrom":[subQ1,subQ0]});Q42=makeQuery(id+"F0.imprint","IMPRINT",FACE,{"disambiguationData":[TD([[makeQuery(id+"F0.imprint","IMPRINT",EDGE,{"disambiguationData":[TD([[subQ2,-1.0]])],"derivedFrom":subQ1}),-1.0]])]});}
            var Q43;
            {var subQ1=sQuery(id+"F0.wireOp",EDGE,"E10.5.2");var subQ3=sQuery(id+"F0.wireOp",EDGE,"E2");var subQ4=makeQuery(id+"F0.imprint","INTERSECT",VERTEX,{"derivedFrom":[subQ3,subQ1]});Q43=makeQuery(id+"F0.imprint","IMPRINT",FACE,{"disambiguationData":[TD([[makeQuery(id+"F0.imprint","IMPRINT",EDGE,{"disambiguationData":[TD([[subQ4,-1.0]])],"derivedFrom":subQ3}),-1.0]])]});}
            var Q44;
            {var subQ0=sQuery(id+"F0.wireOp",EDGE,"E15.8.0");var subQ1=makeQuery(id+"F0.imprint","IMPRINT",VERTEX,{"derivedFrom":subQ0});Q44=makeQuery(id+"F0.imprint","IMPRINT",FACE,{"disambiguationData":[TD([[makeQuery(id+"F0.imprint","IMPRINT",EDGE,{"disambiguationData":[TD([[subQ1,1.0]])],"derivedFrom":subQ0}),-1.0]])]});}
            var Q45;
            {var subQ5=sQuery(id+"F0.wireOp",EDGE,"E10.5.0");var subQ7=sQuery(id+"F0.wireOp",EDGE,"E2");var subQ8=makeQuery(id+"F0.imprint","INTERSECT",VERTEX,{"derivedFrom":[subQ7,subQ5]});Q45=makeQuery(id+"F0.imprint","IMPRINT",FACE,{"disambiguationData":[TD([[makeQuery(id+"F0.imprint","IMPRINT",EDGE,{"disambiguationData":[TD([[subQ8,-1.0]])],"derivedFrom":subQ7}),-1.0]])]});}
            var Q46;
            {var subQ0=sQuery(id+"F0.wireOp",EDGE,"E15.8.0");var subQ1=sQuery(id+"F0.wireOp",EDGE,"E4");var subQ2=makeQuery(id+"F0.imprint","INTERSECT",VERTEX,{"derivedFrom":[subQ1,subQ0]});Q46=makeQuery(id+"F0.imprint","IMPRINT",FACE,{"disambiguationData":[TD([[makeQuery(id+"F0.imprint","IMPRINT",EDGE,{"disambiguationData":[TD([[subQ2,-1.0]])],"derivedFrom":subQ1}),-1.0]])]});}
            var Q47;
            {var subQ3=sQuery(id+"F0.wireOp",EDGE,"E4");var subQ5=sQuery(id+"F0.wireOp",EDGE,"E15.9.0");var subQ6=makeQuery(id+"F0.imprint","INTERSECT",VERTEX,{"derivedFrom":[subQ3,subQ5]});Q47=makeQuery(id+"F0.imprint","IMPRINT",FACE,{"disambiguationData":[TD([[makeQuery(id+"F0.imprint","IMPRINT",EDGE,{"disambiguationData":[TD([[subQ6,-1.0]])],"derivedFrom":subQ3}),-1.0]])]});}
            var Q48;
            {var subQ0=sQuery(id+"F0.wireOp",EDGE,"E15.10.0");var subQ1=makeQuery(id+"F0.imprint","IMPRINT",VERTEX,{"derivedFrom":subQ0});Q48=makeQuery(id+"F0.imprint","IMPRINT",FACE,{"disambiguationData":[TD([[makeQuery(id+"F0.imprint","IMPRINT",EDGE,{"disambiguationData":[TD([[subQ1,1.0]])],"derivedFrom":subQ0}),-1.0]])]});}
            var Q49;
            Q49=makeQuery(id+"F0.imprint","IMPRINT",FACE,{"disambiguationData":[TD([[makeQuery(id+"F0.imprint","IMPRINT",EDGE,{"derivedFrom":sQuery(id+"F0.wireOp",EDGE,"E0")}),-1.0]])]});
            var Q50;
            {var subQ0=sQuery(id+"F0.wireOp",EDGE,"E10.5.2");var subQ1=sQuery(id+"F0.wireOp",EDGE,"E1.0");var subQ2=makeQuery(id+"F0.imprint","INTERSECT",VERTEX,{"derivedFrom":[subQ1,subQ0]});Q50=makeQuery(id+"F0.imprint","IMPRINT",FACE,{"disambiguationData":[TD([[makeQuery(id+"F0.imprint","IMPRINT",EDGE,{"disambiguationData":[TD([[subQ2,-1.0]])],"derivedFrom":subQ1}),-1.0]])]});}
            var Q51;
            {var subQ0=sQuery(id+"F0.wireOp",EDGE,"E10.6.2");var subQ1=sQuery(id+"F0.wireOp",EDGE,"E1.0");var subQ2=makeQuery(id+"F0.imprint","INTERSECT",VERTEX,{"derivedFrom":[subQ1,subQ0]});Q51=makeQuery(id+"F0.imprint","IMPRINT",FACE,{"disambiguationData":[TD([[makeQuery(id+"F0.imprint","IMPRINT",EDGE,{"disambiguationData":[TD([[subQ2,-1.0]])],"derivedFrom":subQ1}),-1.0]])]});}
            var Q52;
            {var subQ0=sQuery(id+"F0.wireOp",EDGE,"E10.7.2");var subQ1=sQuery(id+"F0.wireOp",EDGE,"E1.0");var subQ2=makeQuery(id+"F0.imprint","INTERSECT",VERTEX,{"derivedFrom":[subQ1,subQ0]});Q52=makeQuery(id+"F0.imprint","IMPRINT",FACE,{"disambiguationData":[TD([[makeQuery(id+"F0.imprint","IMPRINT",EDGE,{"disambiguationData":[TD([[subQ2,-1.0]])],"derivedFrom":subQ1}),-1.0]])]});}
            var Q53;
            {var subQ5=sQuery(id+"F0.wireOp",EDGE,"E10.7.0");var subQ7=sQuery(id+"F0.wireOp",EDGE,"E2");var subQ8=makeQuery(id+"F0.imprint","INTERSECT",VERTEX,{"derivedFrom":[subQ7,subQ5]});Q53=makeQuery(id+"F0.imprint","IMPRINT",FACE,{"disambiguationData":[TD([[makeQuery(id+"F0.imprint","IMPRINT",EDGE,{"disambiguationData":[TD([[subQ8,-1.0]])],"derivedFrom":subQ7}),-1.0]])]});}
            var Q54;
            {var subQ5=sQuery(id+"F0.wireOp",EDGE,"E10.8.0");var subQ11=sQuery(id+"F0.wireOp",EDGE,"E2");var subQ12=makeQuery(id+"F0.imprint","INTERSECT",VERTEX,{"derivedFrom":[subQ11,subQ5]});Q54=makeQuery(id+"F0.imprint","IMPRINT",FACE,{"disambiguationData":[TD([[makeQuery(id+"F0.imprint","IMPRINT",EDGE,{"disambiguationData":[TD([[subQ12,-1.0]])],"derivedFrom":subQ11}),-1.0]])]});}
            var Q55;
            {var subQ5=sQuery(id+"F0.wireOp",EDGE,"E10.1.0");var subQ7=sQuery(id+"F0.wireOp",EDGE,"E2");var subQ8=makeQuery(id+"F0.imprint","INTERSECT",VERTEX,{"derivedFrom":[subQ7,subQ5]});Q55=makeQuery(id+"F0.imprint","IMPRINT",FACE,{"disambiguationData":[TD([[makeQuery(id+"F0.imprint","IMPRINT",EDGE,{"disambiguationData":[TD([[subQ8,-1.0]])],"derivedFrom":subQ7}),-1.0]])]});}
            var Q56;
            {var subQ4=sQuery(id+"F0.wireOp",EDGE,"E10.2.0");var subQ5=sQuery(id+"F0.wireOp",EDGE,"E2");var subQ6=makeQuery(id+"F0.imprint","INTERSECT",VERTEX,{"derivedFrom":[subQ5,subQ4]});Q56=makeQuery(id+"F0.imprint","IMPRINT",FACE,{"disambiguationData":[TD([[makeQuery(id+"F0.imprint","IMPRINT",EDGE,{"disambiguationData":[TD([[subQ6,-1.0]])],"derivedFrom":subQ5}),-1.0]])]});}
            var Q57;
            {var subQ5=sQuery(id+"F0.wireOp",EDGE,"E10.3.0");var subQ7=sQuery(id+"F0.wireOp",EDGE,"E2");var subQ8=makeQuery(id+"F0.imprint","INTERSECT",VERTEX,{"derivedFrom":[subQ7,subQ5]});Q57=makeQuery(id+"F0.imprint","IMPRINT",FACE,{"disambiguationData":[TD([[makeQuery(id+"F0.imprint","IMPRINT",EDGE,{"disambiguationData":[TD([[subQ8,-1.0]])],"derivedFrom":subQ7}),-1.0]])]});}
            var Q58;
            {var subQ0=sQuery(id+"F0.wireOp",EDGE,"E15.5.1");var subQ1=sQuery(id+"F0.wireOp",EDGE,"E3.0");var subQ2=makeQuery(id+"F0.imprint","INTERSECT",VERTEX,{"derivedFrom":[subQ1,subQ0]});Q58=makeQuery(id+"F0.imprint","IMPRINT",FACE,{"disambiguationData":[TD([[makeQuery(id+"F0.imprint","IMPRINT",EDGE,{"disambiguationData":[TD([[subQ2,-1.0]])],"derivedFrom":subQ1}),-1.0]])]});}
            var Q59;
            {var subQ0=sQuery(id+"F0.wireOp",EDGE,"E15.4.0");var subQ3=sQuery(id+"F0.wireOp",EDGE,"E4");var subQ4=makeQuery(id+"F0.imprint","INTERSECT",VERTEX,{"derivedFrom":[subQ3,subQ0]});Q59=makeQuery(id+"F0.imprint","IMPRINT",FACE,{"disambiguationData":[TD([[makeQuery(id+"F0.imprint","IMPRINT",EDGE,{"disambiguationData":[TD([[subQ4,-1.0]])],"derivedFrom":subQ3}),-1.0]])]});}
            var Q60;
            {var subQ0=sQuery(id+"F0.wireOp",EDGE,"E15.3.0");var subQ1=sQuery(id+"F0.wireOp",EDGE,"E4");var subQ2=makeQuery(id+"F0.imprint","INTERSECT",VERTEX,{"derivedFrom":[subQ1,subQ0]});Q60=makeQuery(id+"F0.imprint","IMPRINT",FACE,{"disambiguationData":[TD([[makeQuery(id+"F0.imprint","IMPRINT",EDGE,{"disambiguationData":[TD([[subQ2,-1.0]])],"derivedFrom":subQ1}),-1.0]])]});}
            var Q61;
            {var subQ0=sQuery(id+"F0.wireOp",EDGE,"E15.2.0");var subQ1=makeQuery(id+"F0.imprint","IMPRINT",VERTEX,{"derivedFrom":subQ0});Q61=makeQuery(id+"F0.imprint","IMPRINT",FACE,{"disambiguationData":[TD([[makeQuery(id+"F0.imprint","IMPRINT",EDGE,{"disambiguationData":[TD([[subQ1,1.0]])],"derivedFrom":subQ0}),-1.0]])]});}
            var Q62;
            {var subQ0=sQuery(id+"F0.wireOp",EDGE,"E10.2.2");var subQ1=sQuery(id+"F0.wireOp",EDGE,"E1.0");var subQ2=makeQuery(id+"F0.imprint","INTERSECT",VERTEX,{"derivedFrom":[subQ1,subQ0]});Q62=makeQuery(id+"F0.imprint","IMPRINT",FACE,{"disambiguationData":[TD([[makeQuery(id+"F0.imprint","IMPRINT",EDGE,{"disambiguationData":[TD([[subQ2,-1.0]])],"derivedFrom":subQ1}),-1.0]])]});}
            var Q63;
            {var subQ0=sQuery(id+"F0.wireOp",EDGE,"E10.3.2");var subQ1=sQuery(id+"F0.wireOp",EDGE,"E1.0");var subQ2=makeQuery(id+"F0.imprint","INTERSECT",VERTEX,{"derivedFrom":[subQ1,subQ0]});Q63=makeQuery(id+"F0.imprint","IMPRINT",FACE,{"disambiguationData":[TD([[makeQuery(id+"F0.imprint","IMPRINT",EDGE,{"disambiguationData":[TD([[subQ2,-1.0]])],"derivedFrom":subQ1}),-1.0]])]});}
            var Q64;
            {var subQ0=sQuery(id+"F0.wireOp",EDGE,"E15.1.0");var subQ3=sQuery(id+"F0.wireOp",EDGE,"E4");var subQ4=makeQuery(id+"F0.imprint","INTERSECT",VERTEX,{"derivedFrom":[subQ3,subQ0]});Q64=makeQuery(id+"F0.imprint","IMPRINT",FACE,{"disambiguationData":[TD([[makeQuery(id+"F0.imprint","IMPRINT",EDGE,{"disambiguationData":[TD([[subQ4,-1.0]])],"derivedFrom":subQ3}),-1.0]])]});}
            var Q65;
            {var subQ0=sQuery(id+"F0.wireOp",EDGE,"E15.1.1");var subQ1=sQuery(id+"F0.wireOp",EDGE,"E3.0");var subQ2=makeQuery(id+"F0.imprint","INTERSECT",VERTEX,{"derivedFrom":[subQ1,subQ0]});Q65=makeQuery(id+"F0.imprint","IMPRINT",FACE,{"disambiguationData":[TD([[makeQuery(id+"F0.imprint","IMPRINT",EDGE,{"disambiguationData":[TD([[subQ2,-1.0]])],"derivedFrom":subQ1}),-1.0]])]});}
            var Q66;
            {var subQ3=sQuery(id+"F0.wireOp",EDGE,"E4");var subQ5=sQuery(id+"F0.wireOp",EDGE,"E14.0");var subQ6=makeQuery(id+"F0.imprint","INTERSECT",VERTEX,{"derivedFrom":[subQ3,subQ5]});Q66=makeQuery(id+"F0.imprint","IMPRINT",FACE,{"disambiguationData":[TD([[makeQuery(id+"F0.imprint","IMPRINT",EDGE,{"disambiguationData":[TD([[subQ6,-1.0]])],"derivedFrom":subQ3}),-1.0]])]});}
            var Q67;
            {var subQ0=sQuery(id+"F0.wireOp",EDGE,"E15.17.0");var subQ1=sQuery(id+"F0.wireOp",EDGE,"E4");var subQ2=makeQuery(id+"F0.imprint","INTERSECT",VERTEX,{"derivedFrom":[subQ1,subQ0]});Q67=makeQuery(id+"F0.imprint","IMPRINT",FACE,{"disambiguationData":[TD([[makeQuery(id+"F0.imprint","IMPRINT",EDGE,{"disambiguationData":[TD([[subQ2,-1.0]])],"derivedFrom":subQ1}),-1.0]])]});}
            var Q68;
            {var subQ0=sQuery(id+"F0.wireOp",EDGE,"E15.17.1");var subQ5=sQuery(id+"F0.wireOp",EDGE,"E4");var subQ6=makeQuery(id+"F0.imprint","INTERSECT",VERTEX,{"derivedFrom":[subQ5,subQ0]});Q68=makeQuery(id+"F0.imprint","IMPRINT",FACE,{"disambiguationData":[TD([[makeQuery(id+"F0.imprint","IMPRINT",EDGE,{"disambiguationData":[TD([[subQ6,1.0]])],"derivedFrom":subQ5}),-1.0]])]});}
            var Q69;
            {var subQ3=sQuery(id+"F0.wireOp",EDGE,"E4");var subQ5=sQuery(id+"F0.wireOp",EDGE,"E15.15.0");var subQ6=makeQuery(id+"F0.imprint","INTERSECT",VERTEX,{"derivedFrom":[subQ3,subQ5]});Q69=makeQuery(id+"F0.imprint","IMPRINT",FACE,{"disambiguationData":[TD([[makeQuery(id+"F0.imprint","IMPRINT",EDGE,{"disambiguationData":[TD([[subQ6,-1.0]])],"derivedFrom":subQ3}),-1.0]])]});}
            var Q70;
            {var subQ0=sQuery(id+"F0.wireOp",EDGE,"E15.14.0");var subQ1=sQuery(id+"F0.wireOp",EDGE,"E4");var subQ2=makeQuery(id+"F0.imprint","INTERSECT",VERTEX,{"derivedFrom":[subQ1,subQ0]});Q70=makeQuery(id+"F0.imprint","IMPRINT",FACE,{"disambiguationData":[TD([[makeQuery(id+"F0.imprint","IMPRINT",EDGE,{"disambiguationData":[TD([[subQ2,-1.0]])],"derivedFrom":subQ1}),-1.0]])]});}
            var Q71;
            {var subQ0=sQuery(id+"F0.wireOp",EDGE,"E15.13.0");var subQ3=sQuery(id+"F0.wireOp",EDGE,"E4");var subQ4=makeQuery(id+"F0.imprint","INTERSECT",VERTEX,{"derivedFrom":[subQ3,subQ0]});Q71=makeQuery(id+"F0.imprint","IMPRINT",FACE,{"disambiguationData":[TD([[makeQuery(id+"F0.imprint","IMPRINT",EDGE,{"disambiguationData":[TD([[subQ4,-1.0]])],"derivedFrom":subQ3}),-1.0]])]});}
            var Q72;
            {var subQ3=sQuery(id+"F0.wireOp",EDGE,"E4");var subQ5=sQuery(id+"F0.wireOp",EDGE,"E15.12.0");var subQ6=makeQuery(id+"F0.imprint","INTERSECT",VERTEX,{"derivedFrom":[subQ3,subQ5]});Q72=makeQuery(id+"F0.imprint","IMPRINT",FACE,{"disambiguationData":[TD([[makeQuery(id+"F0.imprint","IMPRINT",EDGE,{"disambiguationData":[TD([[subQ6,-1.0]])],"derivedFrom":subQ3}),-1.0]])]});}
            var Q73;
            {var subQ0=sQuery(id+"F0.wireOp",EDGE,"E15.11.0");var subQ1=sQuery(id+"F0.wireOp",EDGE,"E4");var subQ2=makeQuery(id+"F0.imprint","INTERSECT",VERTEX,{"derivedFrom":[subQ1,subQ0]});Q73=makeQuery(id+"F0.imprint","IMPRINT",FACE,{"disambiguationData":[TD([[makeQuery(id+"F0.imprint","IMPRINT",EDGE,{"disambiguationData":[TD([[subQ2,-1.0]])],"derivedFrom":subQ1}),-1.0]])]});}
            var Q74;
            {var subQ0=sQuery(id+"F0.wireOp",EDGE,"E15.10.0");var subQ3=sQuery(id+"F0.wireOp",EDGE,"E4");var subQ4=makeQuery(id+"F0.imprint","INTERSECT",VERTEX,{"derivedFrom":[subQ3,subQ0]});Q74=makeQuery(id+"F0.imprint","IMPRINT",FACE,{"disambiguationData":[TD([[makeQuery(id+"F0.imprint","IMPRINT",EDGE,{"disambiguationData":[TD([[subQ4,-1.0]])],"derivedFrom":subQ3}),-1.0]])]});}
            var Q75;
            {var subQ7=sQuery(id+"F0.wireOp",EDGE,"E10.6.0");var subQ8=sQuery(id+"F0.wireOp",EDGE,"E2");var subQ9=makeQuery(id+"F0.imprint","INTERSECT",VERTEX,{"derivedFrom":[subQ8,subQ7]});Q75=makeQuery(id+"F0.imprint","IMPRINT",FACE,{"disambiguationData":[TD([[makeQuery(id+"F0.imprint","IMPRINT",EDGE,{"disambiguationData":[TD([[subQ9,-1.0]])],"derivedFrom":subQ8}),-1.0]])]});}
            var Q76;
            {var subQ0=sQuery(id+"F0.wireOp",EDGE,"E15.9.1");var subQ1=sQuery(id+"F0.wireOp",EDGE,"E3.0");var subQ2=makeQuery(id+"F0.imprint","INTERSECT",VERTEX,{"derivedFrom":[subQ1,subQ0]});Q76=makeQuery(id+"F0.imprint","IMPRINT",FACE,{"disambiguationData":[TD([[makeQuery(id+"F0.imprint","IMPRINT",EDGE,{"disambiguationData":[TD([[subQ2,-1.0]])],"derivedFrom":subQ1}),-1.0]])]});}
            var Q77;
            {var subQ0=sQuery(id+"F0.wireOp",EDGE,"E15.11.1");var subQ1=sQuery(id+"F0.wireOp",EDGE,"E3.0");var subQ2=makeQuery(id+"F0.imprint","INTERSECT",VERTEX,{"derivedFrom":[subQ1,subQ0]});Q77=makeQuery(id+"F0.imprint","IMPRINT",FACE,{"disambiguationData":[TD([[makeQuery(id+"F0.imprint","IMPRINT",EDGE,{"disambiguationData":[TD([[subQ2,-1.0]])],"derivedFrom":subQ1}),-1.0]])]});}
            var Q78;
            {var subQ0=sQuery(id+"F0.wireOp",EDGE,"E15.12.0");var subQ1=makeQuery(id+"F0.imprint","IMPRINT",VERTEX,{"derivedFrom":subQ0});Q78=makeQuery(id+"F0.imprint","IMPRINT",FACE,{"disambiguationData":[TD([[makeQuery(id+"F0.imprint","IMPRINT",EDGE,{"disambiguationData":[TD([[subQ1,1.0]])],"derivedFrom":subQ0}),-1.0]])]});}
            var Q79;
            {var subQ0=sQuery(id+"F0.wireOp",EDGE,"E15.13.1");var subQ1=sQuery(id+"F0.wireOp",EDGE,"E3.0");var subQ2=makeQuery(id+"F0.imprint","INTERSECT",VERTEX,{"derivedFrom":[subQ1,subQ0]});Q79=makeQuery(id+"F0.imprint","IMPRINT",FACE,{"disambiguationData":[TD([[makeQuery(id+"F0.imprint","IMPRINT",EDGE,{"disambiguationData":[TD([[subQ2,-1.0]])],"derivedFrom":subQ1}),-1.0]])]});}
            var Q80;
            {var subQ0=sQuery(id+"F0.wireOp",EDGE,"E10.8.2");var subQ1=sQuery(id+"F0.wireOp",EDGE,"E1.0");var subQ2=makeQuery(id+"F0.imprint","INTERSECT",VERTEX,{"derivedFrom":[subQ1,subQ0]});Q80=makeQuery(id+"F0.imprint","IMPRINT",FACE,{"disambiguationData":[TD([[makeQuery(id+"F0.imprint","IMPRINT",EDGE,{"disambiguationData":[TD([[subQ2,-1.0]])],"derivedFrom":subQ1}),-1.0]])]});}
            var Q81;
            {var subQ0=sQuery(id+"F0.wireOp",EDGE,"E10.1.2");var subQ1=sQuery(id+"F0.wireOp",EDGE,"E1.0");var subQ2=makeQuery(id+"F0.imprint","INTERSECT",VERTEX,{"derivedFrom":[subQ1,subQ0]});Q81=makeQuery(id+"F0.imprint","IMPRINT",FACE,{"disambiguationData":[TD([[makeQuery(id+"F0.imprint","IMPRINT",EDGE,{"disambiguationData":[TD([[subQ2,-1.0]])],"derivedFrom":subQ1}),-1.0]])]});}
            var Q82;
            {var subQ0=sQuery(id+"F0.wireOp",EDGE,"E13.0");var subQ1=makeQuery(id+"F0.imprint","IMPRINT",VERTEX,{"derivedFrom":subQ0});Q82=makeQuery(id+"F0.imprint","IMPRINT",FACE,{"disambiguationData":[TD([[makeQuery(id+"F0.imprint","IMPRINT",EDGE,{"disambiguationData":[TD([[subQ1,1.0]])],"derivedFrom":subQ0}),1.0]])]});}
            var Q83;
            {var subQ0=sQuery(id+"F0.wireOp",EDGE,"E15.1.1");var subQ1=sQuery(id+"F0.wireOp",EDGE,"E4");var subQ2=makeQuery(id+"F0.imprint","INTERSECT",VERTEX,{"derivedFrom":[subQ1,subQ0]});Q83=makeQuery(id+"F0.imprint","IMPRINT",FACE,{"disambiguationData":[TD([[makeQuery(id+"F0.imprint","IMPRINT",EDGE,{"disambiguationData":[TD([[subQ2,-1.0]])],"derivedFrom":subQ1}),-1.0]])]});}
            var Q84;
            {var subQ1=sQuery(id+"F0.wireOp",EDGE,"E4");var subQ5=sQuery(id+"F0.wireOp",EDGE,"E13.0");var subQ8=makeQuery(id+"F0.imprint","INTERSECT",VERTEX,{"derivedFrom":[subQ1,subQ5]});Q84=makeQuery(id+"F0.imprint","IMPRINT",FACE,{"disambiguationData":[TD([[makeQuery(id+"F0.imprint","IMPRINT",EDGE,{"disambiguationData":[TD([[subQ8,-1.0]])],"derivedFrom":subQ1}),-1.0]])]});}
            var Q85;
            {var subQ0=sQuery(id+"F0.wireOp",EDGE,"E15.17.1");var subQ1=sQuery(id+"F0.wireOp",EDGE,"E3.0");var subQ2=makeQuery(id+"F0.imprint","INTERSECT",VERTEX,{"derivedFrom":[subQ1,subQ0]});Q85=makeQuery(id+"F0.imprint","IMPRINT",FACE,{"disambiguationData":[TD([[makeQuery(id+"F0.imprint","IMPRINT",EDGE,{"disambiguationData":[TD([[subQ2,-1.0]])],"derivedFrom":subQ1}),-1.0]])]});}
            var Q86;
            {var subQ0=sQuery(id+"F0.wireOp",EDGE,"E15.17.1");var subQ1=sQuery(id+"F0.wireOp",EDGE,"E4");var subQ2=makeQuery(id+"F0.imprint","INTERSECT",VERTEX,{"derivedFrom":[subQ1,subQ0]});Q86=makeQuery(id+"F0.imprint","IMPRINT",FACE,{"disambiguationData":[TD([[makeQuery(id+"F0.imprint","IMPRINT",EDGE,{"disambiguationData":[TD([[subQ2,-1.0]])],"derivedFrom":subQ1}),-1.0]])]});}
            var Q87;
            {var subQ0=sQuery(id+"F0.wireOp",EDGE,"E15.16.0");var subQ6=makeQuery(id+"F0.imprint","IMPRINT",VERTEX,{"derivedFrom":subQ0});Q87=makeQuery(id+"F0.imprint","IMPRINT",FACE,{"disambiguationData":[TD([[makeQuery(id+"F0.imprint","IMPRINT",EDGE,{"disambiguationData":[TD([[subQ6,1.0]])],"derivedFrom":subQ0}),-1.0]])]});}
            var Q88;
            {var subQ0=sQuery(id+"F0.wireOp",EDGE,"E15.16.0");var subQ1=sQuery(id+"F0.wireOp",EDGE,"E4");var subQ2=makeQuery(id+"F0.imprint","INTERSECT",VERTEX,{"derivedFrom":[subQ1,subQ0]});Q88=makeQuery(id+"F0.imprint","IMPRINT",FACE,{"disambiguationData":[TD([[makeQuery(id+"F0.imprint","IMPRINT",EDGE,{"disambiguationData":[TD([[subQ2,1.0]])],"derivedFrom":subQ1}),-1.0]])]});}
            var Q89;
            {var subQ0=sQuery(id+"F0.wireOp",EDGE,"E15.15.1");var subQ1=sQuery(id+"F0.wireOp",EDGE,"E3.0");var subQ2=makeQuery(id+"F0.imprint","INTERSECT",VERTEX,{"derivedFrom":[subQ1,subQ0]});Q89=makeQuery(id+"F0.imprint","IMPRINT",FACE,{"disambiguationData":[TD([[makeQuery(id+"F0.imprint","IMPRINT",EDGE,{"disambiguationData":[TD([[subQ2,-1.0]])],"derivedFrom":subQ1}),-1.0]])]});}
            var Q90;
            {var subQ0=sQuery(id+"F0.wireOp",EDGE,"E15.15.1");var subQ3=sQuery(id+"F0.wireOp",EDGE,"E4");var subQ4=makeQuery(id+"F0.imprint","INTERSECT",VERTEX,{"derivedFrom":[subQ3,subQ0]});Q90=makeQuery(id+"F0.imprint","IMPRINT",FACE,{"disambiguationData":[TD([[makeQuery(id+"F0.imprint","IMPRINT",EDGE,{"disambiguationData":[TD([[subQ4,-1.0]])],"derivedFrom":subQ3}),-1.0]])]});}
            var Q91;
            {var subQ0=sQuery(id+"F0.wireOp",EDGE,"E15.14.1");var subQ1=sQuery(id+"F0.wireOp",EDGE,"E4");var subQ2=makeQuery(id+"F0.imprint","INTERSECT",VERTEX,{"derivedFrom":[subQ1,subQ0]});Q91=makeQuery(id+"F0.imprint","IMPRINT",FACE,{"disambiguationData":[TD([[makeQuery(id+"F0.imprint","IMPRINT",EDGE,{"disambiguationData":[TD([[subQ2,-1.0]])],"derivedFrom":subQ1}),-1.0]])]});}
            var Q92;
            {var subQ0=sQuery(id+"F0.wireOp",EDGE,"E15.13.1");var subQ1=sQuery(id+"F0.wireOp",EDGE,"E4");var subQ2=makeQuery(id+"F0.imprint","INTERSECT",VERTEX,{"derivedFrom":[subQ1,subQ0]});Q92=makeQuery(id+"F0.imprint","IMPRINT",FACE,{"disambiguationData":[TD([[makeQuery(id+"F0.imprint","IMPRINT",EDGE,{"disambiguationData":[TD([[subQ2,-1.0]])],"derivedFrom":subQ1}),-1.0]])]});}
            var Q93;
            {var subQ1=sQuery(id+"F0.wireOp",EDGE,"E4");var subQ5=sQuery(id+"F0.wireOp",EDGE,"E15.12.1");var subQ9=makeQuery(id+"F0.imprint","INTERSECT",VERTEX,{"derivedFrom":[subQ1,subQ5]});Q93=makeQuery(id+"F0.imprint","IMPRINT",FACE,{"disambiguationData":[TD([[makeQuery(id+"F0.imprint","IMPRINT",EDGE,{"disambiguationData":[TD([[subQ9,-1.0]])],"derivedFrom":subQ1}),-1.0]])]});}
            var Q94;
            {var subQ1=sQuery(id+"F0.wireOp",EDGE,"E10.7.2");var subQ3=sQuery(id+"F0.wireOp",EDGE,"E2");var subQ4=makeQuery(id+"F0.imprint","INTERSECT",VERTEX,{"derivedFrom":[subQ3,subQ1]});Q94=makeQuery(id+"F0.imprint","IMPRINT",FACE,{"disambiguationData":[TD([[makeQuery(id+"F0.imprint","IMPRINT",EDGE,{"disambiguationData":[TD([[subQ4,-1.0]])],"derivedFrom":subQ3}),-1.0]])]});}
            var Q95;
            {var subQ0=sQuery(id+"F0.wireOp",EDGE,"E15.11.1");var subQ1=sQuery(id+"F0.wireOp",EDGE,"E4");var subQ2=makeQuery(id+"F0.imprint","INTERSECT",VERTEX,{"derivedFrom":[subQ1,subQ0]});Q95=makeQuery(id+"F0.imprint","IMPRINT",FACE,{"disambiguationData":[TD([[makeQuery(id+"F0.imprint","IMPRINT",EDGE,{"disambiguationData":[TD([[subQ2,-1.0]])],"derivedFrom":subQ1}),-1.0]])]});}
            var Q96;
            {var subQ0=sQuery(id+"F0.wireOp",EDGE,"E15.10.1");var subQ1=sQuery(id+"F0.wireOp",EDGE,"E4");var subQ2=makeQuery(id+"F0.imprint","INTERSECT",VERTEX,{"derivedFrom":[subQ1,subQ0]});Q96=makeQuery(id+"F0.imprint","IMPRINT",FACE,{"disambiguationData":[TD([[makeQuery(id+"F0.imprint","IMPRINT",EDGE,{"disambiguationData":[TD([[subQ2,-1.0]])],"derivedFrom":subQ1}),-1.0]])]});}
            var Q97;
            {var subQ3=sQuery(id+"F0.wireOp",EDGE,"E2");var subQ6=sQuery(id+"F0.wireOp",EDGE,"E10.6.2");var subQ8=makeQuery(id+"F0.imprint","INTERSECT",VERTEX,{"derivedFrom":[subQ3,subQ6]});Q97=makeQuery(id+"F0.imprint","IMPRINT",FACE,{"disambiguationData":[TD([[makeQuery(id+"F0.imprint","IMPRINT",EDGE,{"disambiguationData":[TD([[subQ8,-1.0]])],"derivedFrom":subQ3}),-1.0]])]});}
            var Q98;
            {var subQ0=sQuery(id+"F0.wireOp",EDGE,"E15.9.1");var subQ3=sQuery(id+"F0.wireOp",EDGE,"E4");var subQ4=makeQuery(id+"F0.imprint","INTERSECT",VERTEX,{"derivedFrom":[subQ3,subQ0]});Q98=makeQuery(id+"F0.imprint","IMPRINT",FACE,{"disambiguationData":[TD([[makeQuery(id+"F0.imprint","IMPRINT",EDGE,{"disambiguationData":[TD([[subQ4,-1.0]])],"derivedFrom":subQ3}),-1.0]])]});}
            var Q99;
            {var subQ3=sQuery(id+"F0.wireOp",EDGE,"E2");var subQ9=sQuery(id+"F0.wireOp",EDGE,"E10.3.2");var subQ11=makeQuery(id+"F0.imprint","INTERSECT",VERTEX,{"derivedFrom":[subQ3,subQ9]});Q99=makeQuery(id+"F0.imprint","IMPRINT",FACE,{"disambiguationData":[TD([[makeQuery(id+"F0.imprint","IMPRINT",EDGE,{"disambiguationData":[TD([[subQ11,-1.0]])],"derivedFrom":subQ3}),-1.0]])]});}
            var Q100;
            {var subQ0=sQuery(id+"F0.wireOp",EDGE,"E15.3.1");var subQ3=sQuery(id+"F0.wireOp",EDGE,"E4");var subQ4=makeQuery(id+"F0.imprint","INTERSECT",VERTEX,{"derivedFrom":[subQ3,subQ0]});Q100=makeQuery(id+"F0.imprint","IMPRINT",FACE,{"disambiguationData":[TD([[makeQuery(id+"F0.imprint","IMPRINT",EDGE,{"disambiguationData":[TD([[subQ4,-1.0]])],"derivedFrom":subQ3}),-1.0]])]});}
            var Q101;
            {var subQ0=sQuery(id+"F0.wireOp",EDGE,"E15.2.1");var subQ1=sQuery(id+"F0.wireOp",EDGE,"E4");var subQ2=makeQuery(id+"F0.imprint","INTERSECT",VERTEX,{"derivedFrom":[subQ1,subQ0]});Q101=makeQuery(id+"F0.imprint","IMPRINT",FACE,{"disambiguationData":[TD([[makeQuery(id+"F0.imprint","IMPRINT",EDGE,{"disambiguationData":[TD([[subQ2,-1.0]])],"derivedFrom":subQ1}),-1.0]])]});}
            var Q102;
            {var subQ1=sQuery(id+"F0.wireOp",EDGE,"E10.2.2");var subQ3=sQuery(id+"F0.wireOp",EDGE,"E2");var subQ4=makeQuery(id+"F0.imprint","INTERSECT",VERTEX,{"derivedFrom":[subQ3,subQ1]});Q102=makeQuery(id+"F0.imprint","IMPRINT",FACE,{"disambiguationData":[TD([[makeQuery(id+"F0.imprint","IMPRINT",EDGE,{"disambiguationData":[TD([[subQ4,-1.0]])],"derivedFrom":subQ3}),-1.0]])]});}
            var Q103;
            {var subQ3=sQuery(id+"F0.wireOp",EDGE,"E2");var subQ6=sQuery(id+"F0.wireOp",EDGE,"E10.1.2");var subQ11=makeQuery(id+"F0.imprint","INTERSECT",VERTEX,{"derivedFrom":[subQ3,subQ6]});Q103=makeQuery(id+"F0.imprint","IMPRINT",FACE,{"disambiguationData":[TD([[makeQuery(id+"F0.imprint","IMPRINT",EDGE,{"disambiguationData":[TD([[subQ11,-1.0]])],"derivedFrom":subQ3}),-1.0]])]});}
            var Q104;
            {var subQ0=sQuery(id+"F0.wireOp",EDGE,"E9.0");var subQ1=sQuery(id+"F0.wireOp",EDGE,"E1.0");var subQ2=makeQuery(id+"F0.imprint","INTERSECT",VERTEX,{"derivedFrom":[subQ1,subQ0]});Q104=makeQuery(id+"F0.imprint","IMPRINT",FACE,{"disambiguationData":[TD([[makeQuery(id+"F0.imprint","IMPRINT",EDGE,{"disambiguationData":[TD([[subQ2,1.0]])],"derivedFrom":subQ1}),-1.0]])]});}
            var Q105;
            {var subQ0=sQuery(id+"F0.wireOp",EDGE,"E15.14.0");var subQ1=makeQuery(id+"F0.imprint","IMPRINT",VERTEX,{"derivedFrom":subQ0});Q105=makeQuery(id+"F0.imprint","IMPRINT",FACE,{"disambiguationData":[TD([[makeQuery(id+"F0.imprint","IMPRINT",EDGE,{"disambiguationData":[TD([[subQ1,1.0]])],"derivedFrom":subQ0}),1.0]])]});}
            var Q106;
            {var subQ1=sQuery(id+"F0.wireOp",EDGE,"E10.8.2");var subQ3=sQuery(id+"F0.wireOp",EDGE,"E2");var subQ4=makeQuery(id+"F0.imprint","INTERSECT",VERTEX,{"derivedFrom":[subQ3,subQ1]});Q106=makeQuery(id+"F0.imprint","IMPRINT",FACE,{"disambiguationData":[TD([[makeQuery(id+"F0.imprint","IMPRINT",EDGE,{"disambiguationData":[TD([[subQ4,-1.0]])],"derivedFrom":subQ3}),-1.0]])]});}
            var Q107;
            {var subQ1=sQuery(id+"F0.wireOp",EDGE,"E9.0");var subQ3=sQuery(id+"F0.wireOp",EDGE,"E2");var subQ4=makeQuery(id+"F0.imprint","INTERSECT",VERTEX,{"derivedFrom":[subQ3,subQ1]});Q107=makeQuery(id+"F0.imprint","IMPRINT",FACE,{"disambiguationData":[TD([[makeQuery(id+"F0.imprint","IMPRINT",EDGE,{"disambiguationData":[TD([[subQ4,1.0]])],"derivedFrom":subQ3}),-1.0]])]});}
            var Q108;
            {var subQ7=sQuery(id+"F0.wireOp",EDGE,"E10.1.2");var subQ8=sQuery(id+"F0.wireOp",EDGE,"E2");var subQ9=makeQuery(id+"F0.imprint","INTERSECT",VERTEX,{"derivedFrom":[subQ8,subQ7]});Q108=makeQuery(id+"F0.imprint","IMPRINT",FACE,{"disambiguationData":[TD([[makeQuery(id+"F0.imprint","IMPRINT",EDGE,{"disambiguationData":[TD([[subQ9,1.0]])],"derivedFrom":subQ8}),-1.0]])]});}
            var Q109;
            {var subQ0=sQuery(id+"F0.wireOp",EDGE,"E15.14.0");var subQ1=makeQuery(id+"F0.imprint","IMPRINT",VERTEX,{"derivedFrom":subQ0});Q109=makeQuery(id+"F0.imprint","IMPRINT",FACE,{"disambiguationData":[TD([[makeQuery(id+"F0.imprint","IMPRINT",EDGE,{"disambiguationData":[TD([[subQ1,1.0]])],"derivedFrom":subQ0}),-1.0]])]});}
            var Q110;
            {var subQ0=sQuery(id+"F0.wireOp",EDGE,"E5.0");var subQ1=makeQuery(id+"F0.imprint","INTERSECT",VERTEX,{"derivedFrom":[subQ0,sQuery(id+"F0.wireOp",EDGE,"E15.9.0")]});Q110=makeQuery(id+"F0.imprint","IMPRINT",FACE,{"disambiguationData":[TD([[makeQuery(id+"F0.imprint","IMPRINT",EDGE,{"disambiguationData":[TD([[subQ1,1.0]])],"derivedFrom":subQ0}),-1.0]])]});}
            var Q111;
            {var subQ0=sQuery(id+"F0.wireOp",EDGE,"E15.9.0");var subQ1=sQuery(id+"F0.wireOp",EDGE,"E5.0");var subQ2=makeQuery(id+"F0.imprint","INTERSECT",VERTEX,{"derivedFrom":[subQ1,subQ0]});Q111=makeQuery(id+"F0.imprint","IMPRINT",FACE,{"disambiguationData":[TD([[makeQuery(id+"F0.imprint","IMPRINT",EDGE,{"disambiguationData":[TD([[subQ2,-1.0]])],"derivedFrom":subQ1}),1.0]])]});}
            var Q112;
            {var subQ0=sQuery(id+"F0.wireOp",EDGE,"E15.9.0");var subQ1=sQuery(id+"F0.wireOp",EDGE,"E5.0");var subQ2=makeQuery(id+"F0.imprint","INTERSECT",VERTEX,{"derivedFrom":[subQ1,subQ0]});Q112=makeQuery(id+"F0.imprint","IMPRINT",FACE,{"disambiguationData":[TD([[makeQuery(id+"F0.imprint","IMPRINT",EDGE,{"disambiguationData":[TD([[subQ2,1.0]])],"derivedFrom":subQ1}),1.0]])]});}
            var Q113;
            {var subQ0=sQuery(id+"F0.wireOp",EDGE,"E17.6.0");var subQ1=sQuery(id+"F0.wireOp",EDGE,"E5.0");var subQ2=makeQuery(id+"F0.imprint","INTERSECT",VERTEX,{"disambiguationData":[OD(0.0)],"derivedFrom":[subQ1,subQ0]});Q113=makeQuery(id+"F0.imprint","IMPRINT",FACE,{"disambiguationData":[TD([[makeQuery(id+"F0.imprint","IMPRINT",EDGE,{"disambiguationData":[TD([[subQ2,-1.0]])],"derivedFrom":subQ1}),1.0]])]});}
            var Q114;
            {var subQ0=sQuery(id+"F0.wireOp",EDGE,"E17.6.0");var subQ1=sQuery(id+"F0.wireOp",EDGE,"E5.0");var subQ2=makeQuery(id+"F0.imprint","INTERSECT",VERTEX,{"disambiguationData":[OD(0.0)],"derivedFrom":[subQ1,subQ0]});Q114=makeQuery(id+"F0.imprint","IMPRINT",FACE,{"disambiguationData":[TD([[makeQuery(id+"F0.imprint","IMPRINT",EDGE,{"disambiguationData":[TD([[subQ2,-1.0]])],"derivedFrom":subQ1}),-1.0]])]});}
            var Q115;
            {var subQ0=sQuery(id+"F0.wireOp",EDGE,"E17.8.0");var subQ1=sQuery(id+"F0.wireOp",EDGE,"E5.0");var subQ2=makeQuery(id+"F0.imprint","INTERSECT",VERTEX,{"disambiguationData":[OD(0.0)],"derivedFrom":[subQ1,subQ0]});Q115=makeQuery(id+"F0.imprint","IMPRINT",FACE,{"disambiguationData":[TD([[makeQuery(id+"F0.imprint","IMPRINT",EDGE,{"disambiguationData":[TD([[subQ2,-1.0]])],"derivedFrom":subQ1}),1.0]])]});}
            var Q116;
            {var subQ0=sQuery(id+"F0.wireOp",EDGE,"E17.8.0");var subQ1=sQuery(id+"F0.wireOp",EDGE,"E5.0");var subQ2=makeQuery(id+"F0.imprint","INTERSECT",VERTEX,{"disambiguationData":[OD(0.0)],"derivedFrom":[subQ1,subQ0]});Q116=makeQuery(id+"F0.imprint","IMPRINT",FACE,{"disambiguationData":[TD([[makeQuery(id+"F0.imprint","IMPRINT",EDGE,{"disambiguationData":[TD([[subQ2,-1.0]])],"derivedFrom":subQ1}),-1.0]])]});}
            var Q117;
            {var subQ0=sQuery(id+"F0.wireOp",EDGE,"E5.0");var subQ1=makeQuery(id+"F0.imprint","INTERSECT",VERTEX,{"derivedFrom":[subQ0,sQuery(id+"F0.wireOp",EDGE,"E15.6.0")]});Q117=makeQuery(id+"F0.imprint","IMPRINT",FACE,{"disambiguationData":[TD([[makeQuery(id+"F0.imprint","IMPRINT",EDGE,{"disambiguationData":[TD([[subQ1,1.0]])],"derivedFrom":subQ0}),-1.0]])]});}
            var Q118;
            {var subQ0=sQuery(id+"F0.wireOp",EDGE,"E15.6.0");var subQ1=sQuery(id+"F0.wireOp",EDGE,"E5.0");var subQ2=makeQuery(id+"F0.imprint","INTERSECT",VERTEX,{"derivedFrom":[subQ1,subQ0]});Q118=makeQuery(id+"F0.imprint","IMPRINT",FACE,{"disambiguationData":[TD([[makeQuery(id+"F0.imprint","IMPRINT",EDGE,{"disambiguationData":[TD([[subQ2,-1.0]])],"derivedFrom":subQ1}),1.0]])]});}
            var Q119;
            {var subQ0=sQuery(id+"F0.wireOp",EDGE,"E15.6.0");var subQ1=sQuery(id+"F0.wireOp",EDGE,"E5.0");var subQ2=makeQuery(id+"F0.imprint","INTERSECT",VERTEX,{"derivedFrom":[subQ1,subQ0]});Q119=makeQuery(id+"F0.imprint","IMPRINT",FACE,{"disambiguationData":[TD([[makeQuery(id+"F0.imprint","IMPRINT",EDGE,{"disambiguationData":[TD([[subQ2,1.0]])],"derivedFrom":subQ1}),1.0]])]});}
            var Q120;
            {var subQ0=sQuery(id+"F0.wireOp",EDGE,"E17.4.0");var subQ1=sQuery(id+"F0.wireOp",EDGE,"E5.0");var subQ2=makeQuery(id+"F0.imprint","INTERSECT",VERTEX,{"disambiguationData":[OD(0.0)],"derivedFrom":[subQ1,subQ0]});Q120=makeQuery(id+"F0.imprint","IMPRINT",FACE,{"disambiguationData":[TD([[makeQuery(id+"F0.imprint","IMPRINT",EDGE,{"disambiguationData":[TD([[subQ2,-1.0]])],"derivedFrom":subQ1}),-1.0]])]});}
            var Q121;
            {var subQ0=sQuery(id+"F0.wireOp",EDGE,"E17.4.0");var subQ1=sQuery(id+"F0.wireOp",EDGE,"E5.0");var subQ2=makeQuery(id+"F0.imprint","INTERSECT",VERTEX,{"disambiguationData":[OD(0.0)],"derivedFrom":[subQ1,subQ0]});Q121=makeQuery(id+"F0.imprint","IMPRINT",FACE,{"disambiguationData":[TD([[makeQuery(id+"F0.imprint","IMPRINT",EDGE,{"disambiguationData":[TD([[subQ2,-1.0]])],"derivedFrom":subQ1}),1.0]])]});}
            var Q122;
            {var subQ0=sQuery(id+"F0.wireOp",EDGE,"E15.3.0");var subQ1=sQuery(id+"F0.wireOp",EDGE,"E5.0");var subQ2=makeQuery(id+"F0.imprint","INTERSECT",VERTEX,{"derivedFrom":[subQ1,subQ0]});Q122=makeQuery(id+"F0.imprint","IMPRINT",FACE,{"disambiguationData":[TD([[makeQuery(id+"F0.imprint","IMPRINT",EDGE,{"disambiguationData":[TD([[subQ2,-1.0]])],"derivedFrom":subQ1}),1.0]])]});}
            var Q123;
            {var subQ0=sQuery(id+"F0.wireOp",EDGE,"E15.3.0");var subQ1=sQuery(id+"F0.wireOp",EDGE,"E5.0");var subQ2=makeQuery(id+"F0.imprint","INTERSECT",VERTEX,{"derivedFrom":[subQ1,subQ0]});Q123=makeQuery(id+"F0.imprint","IMPRINT",FACE,{"disambiguationData":[TD([[makeQuery(id+"F0.imprint","IMPRINT",EDGE,{"disambiguationData":[TD([[subQ2,1.0]])],"derivedFrom":subQ1}),1.0]])]});}
            var Q124;
            {var subQ0=sQuery(id+"F0.wireOp",EDGE,"E5.0");var subQ1=makeQuery(id+"F0.imprint","INTERSECT",VERTEX,{"derivedFrom":[subQ0,sQuery(id+"F0.wireOp",EDGE,"E15.3.0")]});Q124=makeQuery(id+"F0.imprint","IMPRINT",FACE,{"disambiguationData":[TD([[makeQuery(id+"F0.imprint","IMPRINT",EDGE,{"disambiguationData":[TD([[subQ1,1.0]])],"derivedFrom":subQ0}),-1.0]])]});}
            var Q125;
            {var subQ0=sQuery(id+"F0.wireOp",EDGE,"E17.2.0");var subQ1=sQuery(id+"F0.wireOp",EDGE,"E5.0");var subQ2=makeQuery(id+"F0.imprint","INTERSECT",VERTEX,{"disambiguationData":[OD(0.0)],"derivedFrom":[subQ1,subQ0]});Q125=makeQuery(id+"F0.imprint","IMPRINT",FACE,{"disambiguationData":[TD([[makeQuery(id+"F0.imprint","IMPRINT",EDGE,{"disambiguationData":[TD([[subQ2,-1.0]])],"derivedFrom":subQ1}),-1.0]])]});}
            var Q126;
            {var subQ0=sQuery(id+"F0.wireOp",EDGE,"E17.2.0");var subQ1=sQuery(id+"F0.wireOp",EDGE,"E5.0");var subQ2=makeQuery(id+"F0.imprint","INTERSECT",VERTEX,{"disambiguationData":[OD(0.0)],"derivedFrom":[subQ1,subQ0]});Q126=makeQuery(id+"F0.imprint","IMPRINT",FACE,{"disambiguationData":[TD([[makeQuery(id+"F0.imprint","IMPRINT",EDGE,{"disambiguationData":[TD([[subQ2,-1.0]])],"derivedFrom":subQ1}),1.0]])]});}
            var Q127;
            {var subQ0=sQuery(id+"F0.wireOp",EDGE,"E5.0");var subQ1=makeQuery(id+"F0.imprint","INTERSECT",VERTEX,{"derivedFrom":[subQ0,sQuery(id+"F0.wireOp",EDGE,"E14.0")]});Q127=makeQuery(id+"F0.imprint","IMPRINT",FACE,{"disambiguationData":[TD([[makeQuery(id+"F0.imprint","IMPRINT",EDGE,{"disambiguationData":[TD([[subQ1,1.0]])],"derivedFrom":subQ0}),-1.0]])]});}
            var Q128;
            {var subQ0=sQuery(id+"F0.wireOp",EDGE,"E14.0");var subQ1=sQuery(id+"F0.wireOp",EDGE,"E5.0");var subQ2=makeQuery(id+"F0.imprint","INTERSECT",VERTEX,{"derivedFrom":[subQ1,subQ0]});Q128=makeQuery(id+"F0.imprint","IMPRINT",FACE,{"disambiguationData":[TD([[makeQuery(id+"F0.imprint","IMPRINT",EDGE,{"disambiguationData":[TD([[subQ2,1.0]])],"derivedFrom":subQ1}),1.0]])]});}
            var Q129;
            {var subQ0=sQuery(id+"F0.wireOp",EDGE,"E16");var subQ1=sQuery(id+"F0.wireOp",EDGE,"E5.0");var subQ2=makeQuery(id+"F0.imprint","INTERSECT",VERTEX,{"disambiguationData":[OD(0.0)],"derivedFrom":[subQ1,subQ0]});Q129=makeQuery(id+"F0.imprint","IMPRINT",FACE,{"disambiguationData":[TD([[makeQuery(id+"F0.imprint","IMPRINT",EDGE,{"disambiguationData":[TD([[subQ2,-1.0]])],"derivedFrom":subQ1}),-1.0]])]});}
            var Q130;
            {var subQ0=sQuery(id+"F0.wireOp",EDGE,"E16");var subQ1=sQuery(id+"F0.wireOp",EDGE,"E5.0");var subQ2=makeQuery(id+"F0.imprint","INTERSECT",VERTEX,{"disambiguationData":[OD(0.0)],"derivedFrom":[subQ1,subQ0]});Q130=makeQuery(id+"F0.imprint","IMPRINT",FACE,{"disambiguationData":[TD([[makeQuery(id+"F0.imprint","IMPRINT",EDGE,{"disambiguationData":[TD([[subQ2,-1.0]])],"derivedFrom":subQ1}),1.0]])]});}
            var Q131;
            {var subQ0=sQuery(id+"F0.wireOp",EDGE,"E5.0");var subQ1=makeQuery(id+"F0.imprint","INTERSECT",VERTEX,{"derivedFrom":[subQ0,sQuery(id+"F0.wireOp",EDGE,"E15.15.0")]});Q131=makeQuery(id+"F0.imprint","IMPRINT",FACE,{"disambiguationData":[TD([[makeQuery(id+"F0.imprint","IMPRINT",EDGE,{"disambiguationData":[TD([[subQ1,1.0]])],"derivedFrom":subQ0}),-1.0]])]});}
            var Q132;
            {var subQ0=sQuery(id+"F0.wireOp",EDGE,"E15.15.0");var subQ1=sQuery(id+"F0.wireOp",EDGE,"E5.0");var subQ2=makeQuery(id+"F0.imprint","INTERSECT",VERTEX,{"derivedFrom":[subQ1,subQ0]});Q132=makeQuery(id+"F0.imprint","IMPRINT",FACE,{"disambiguationData":[TD([[makeQuery(id+"F0.imprint","IMPRINT",EDGE,{"disambiguationData":[TD([[subQ2,1.0]])],"derivedFrom":subQ1}),1.0]])]});}
            var Q133;
            {var subQ0=sQuery(id+"F0.wireOp",EDGE,"E15.15.0");var subQ1=sQuery(id+"F0.wireOp",EDGE,"E5.0");var subQ2=makeQuery(id+"F0.imprint","INTERSECT",VERTEX,{"derivedFrom":[subQ1,subQ0]});Q133=makeQuery(id+"F0.imprint","IMPRINT",FACE,{"disambiguationData":[TD([[makeQuery(id+"F0.imprint","IMPRINT",EDGE,{"disambiguationData":[TD([[subQ2,-1.0]])],"derivedFrom":subQ1}),1.0]])]});}
            var Q134;
            {var subQ0=sQuery(id+"F0.wireOp",EDGE,"E17.10.0");var subQ1=sQuery(id+"F0.wireOp",EDGE,"E5.0");var subQ2=makeQuery(id+"F0.imprint","INTERSECT",VERTEX,{"disambiguationData":[OD(0.0)],"derivedFrom":[subQ1,subQ0]});Q134=makeQuery(id+"F0.imprint","IMPRINT",FACE,{"disambiguationData":[TD([[makeQuery(id+"F0.imprint","IMPRINT",EDGE,{"disambiguationData":[TD([[subQ2,-1.0]])],"derivedFrom":subQ1}),-1.0]])]});}
            var Q135;
            {var subQ0=sQuery(id+"F0.wireOp",EDGE,"E17.10.0");var subQ1=sQuery(id+"F0.wireOp",EDGE,"E5.0");var subQ2=makeQuery(id+"F0.imprint","INTERSECT",VERTEX,{"disambiguationData":[OD(0.0)],"derivedFrom":[subQ1,subQ0]});Q135=makeQuery(id+"F0.imprint","IMPRINT",FACE,{"disambiguationData":[TD([[makeQuery(id+"F0.imprint","IMPRINT",EDGE,{"disambiguationData":[TD([[subQ2,-1.0]])],"derivedFrom":subQ1}),1.0]])]});}
            var Q136;
            {var subQ0=sQuery(id+"F0.wireOp",EDGE,"E5.0");var subQ1=makeQuery(id+"F0.imprint","INTERSECT",VERTEX,{"derivedFrom":[subQ0,sQuery(id+"F0.wireOp",EDGE,"E15.12.0")]});Q136=makeQuery(id+"F0.imprint","IMPRINT",FACE,{"disambiguationData":[TD([[makeQuery(id+"F0.imprint","IMPRINT",EDGE,{"disambiguationData":[TD([[subQ1,1.0]])],"derivedFrom":subQ0}),-1.0]])]});}
            var Q137;
            {var subQ0=sQuery(id+"F0.wireOp",EDGE,"E15.12.0");var subQ1=sQuery(id+"F0.wireOp",EDGE,"E5.0");var subQ2=makeQuery(id+"F0.imprint","INTERSECT",VERTEX,{"derivedFrom":[subQ1,subQ0]});Q137=makeQuery(id+"F0.imprint","IMPRINT",FACE,{"disambiguationData":[TD([[makeQuery(id+"F0.imprint","IMPRINT",EDGE,{"disambiguationData":[TD([[subQ2,1.0]])],"derivedFrom":subQ1}),1.0]])]});}
            var Q138;
            {var subQ0=sQuery(id+"F0.wireOp",EDGE,"E15.12.0");var subQ1=sQuery(id+"F0.wireOp",EDGE,"E5.0");var subQ2=makeQuery(id+"F0.imprint","INTERSECT",VERTEX,{"derivedFrom":[subQ1,subQ0]});Q138=makeQuery(id+"F0.imprint","IMPRINT",FACE,{"disambiguationData":[TD([[makeQuery(id+"F0.imprint","IMPRINT",EDGE,{"disambiguationData":[TD([[subQ2,-1.0]])],"derivedFrom":subQ1}),1.0]])]});}
            var Q139;
            {var subQ0=sQuery(id+"F0.wireOp",EDGE,"E14.0");var subQ1=sQuery(id+"F0.wireOp",EDGE,"E5.0");var subQ2=makeQuery(id+"F0.imprint","INTERSECT",VERTEX,{"derivedFrom":[subQ1,subQ0]});Q139=makeQuery(id+"F0.imprint","IMPRINT",FACE,{"disambiguationData":[TD([[makeQuery(id+"F0.imprint","IMPRINT",EDGE,{"disambiguationData":[TD([[subQ2,-1.0]])],"derivedFrom":subQ1}),1.0]])]});}
            extrude(context, id + "F2", {"entities" : qUnion([Q0, Q1, Q2, Q3, Q4, Q5, Q6, Q7, Q8, Q9, Q10, Q11, Q12, Q13, Q14, Q15, Q16, Q17, Q18, Q19, Q20, Q21, Q22, Q23, Q24, Q25, Q26, Q27, Q28, Q29, Q30, Q31, Q32, Q33, Q34, Q35, Q36, Q37, Q38, Q39, Q40, Q41, Q42, Q43, Q44, Q45, Q46, Q47, Q48, Q49, Q50, Q51, Q52, Q53, Q54, Q55, Q56, Q57, Q58, Q59, Q60, Q61, Q62, Q63, Q64, Q65, Q66, Q67, Q68, Q69, Q70, Q71, Q72, Q73, Q74, Q75, Q76, Q77, Q78, Q79, Q80, Q81, Q82, Q83, Q84, Q85, Q86, Q87, Q88, Q89, Q90, Q91, Q92, Q93, Q94, Q95, Q96, Q97, Q98, Q99, Q100, Q101, Q102, Q103, Q104, Q105, Q106, Q107, Q108, Q109, Q110, Q111, Q112, Q113, Q114, Q115, Q116, Q117, Q118, Q119, Q120, Q121, Q122, Q123, Q124, Q125, Q126, Q127, Q128, Q129, Q130, Q131, Q132, Q133, Q134, Q135, Q136, Q137, Q138, Q139]), "operationType" : NewBodyOperationType.ADD, "oppositeDirection" : true, "depth" : 3 * mm});
        }
    });
